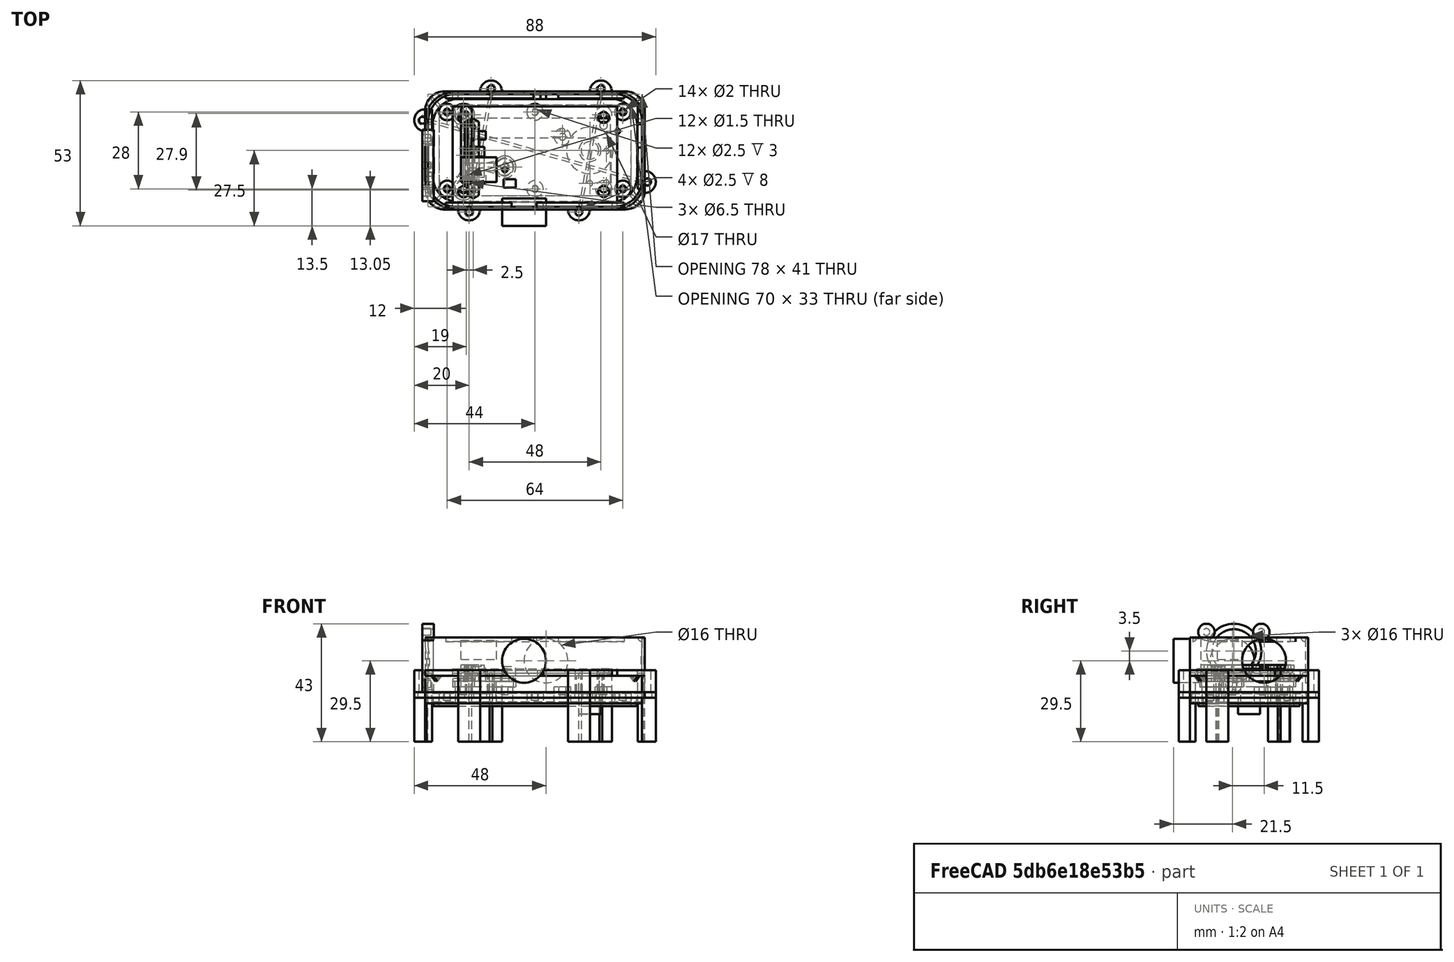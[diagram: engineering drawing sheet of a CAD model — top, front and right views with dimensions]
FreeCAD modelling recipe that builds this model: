
FCSTD DOCUMENT  (FreeCAD 0.18R4 (GitTag))
Label: control_sbox+deckel_166
License: All rights reserved
LicenseURL: http://en.wikipedia.org/wiki/All_rights_reserved
objects: Part::Cylinder×76, PartDesign::Body×49, Sketcher::SketchObject×48, PartDesign::Pad×48, App::DocumentObjectGroup×48, Part::Cut×36, Part::Box×27, App::Part×19, Mesh::Feature×13, Part::MultiFuse×6, PartDesign::Fillet×5
note: 343 computed .brp shape members not serialized (recipe doc carries the construction recipe); baked Part::Feature solids carry a one-line shape summary decoded from their .brp

FEATURE [Sketcher::SketchObject] Sketch001
  sketch-geometry (8):
    g0: LineSegment StartX=11 StartY=1.8e-15 StartZ=0 EndX=69 EndY=1.8e-15 EndZ=0
    g1: LineSegment StartX=80 StartY=11 StartZ=0 EndX=80 EndY=32 EndZ=0
    g2: LineSegment StartX=69 StartY=43 StartZ=0 EndX=11 EndY=43 EndZ=0
    g3: LineSegment StartX=0 StartY=32 StartZ=0 EndX=0 EndY=11 EndZ=0
    g4: ArcOfCircle CenterX=11 CenterY=32 CenterZ=0 NormalX=0 NormalY=0 NormalZ=1 AngleXU=0 Radius=11 StartAngle=1.5708 EndAngle=3.14159
    g5: ArcOfCircle CenterX=11 CenterY=11 CenterZ=0 NormalX=0 NormalY=0 NormalZ=1 AngleXU=0 Radius=11 StartAngle=3.14159 EndAngle=4.71239
    g6: ArcOfCircle CenterX=69 CenterY=32 CenterZ=0 NormalX=0 NormalY=0 NormalZ=1 AngleXU=0 Radius=11 StartAngle=1e-16 EndAngle=1.5708
    g7: ArcOfCircle CenterX=69 CenterY=11 CenterZ=0 NormalX=0 NormalY=0 NormalZ=1 AngleXU=0 Radius=11 StartAngle=4.71239 EndAngle=6.28319
  constraints (20):
    c: Horizontal(g0)
    c: Horizontal(g2)
    c: Vertical(g1)
    c: Vertical(g3)
    c: Tangent(g2,g4) = -1.5708
    c: Tangent(g3,g4) = -1.5708
    c: Tangent(g3,g5) = -1.5708
    c: Tangent(g0,g5) = -1.5708
    c: Radius(g4) = 11
    c: Radius(g5) = 11
    c: Tangent(g2,g6) = -1.5708
    c: Tangent(g1,g6) = -1.5708
    c: Tangent(g1,g7) = -1.5708
    c: Tangent(g0,g7) = -1.5708
    c: Radius(g7) = 11
    c: Radius(g6) = 11
    c: DistanceY(g0,g2) = 43
    c: DistanceX(g3,g1) = 80
    c: DistanceX(g3,g-1) = 0
    c: DistanceY(g-1,g0) = 0
FEATURE [PartDesign::Pad] Pad001
  Length = 1.5
  Length2 = 100
  Profile = -> Sketch001
  Type = 0
FEATURE [Part::Cylinder] Cylinder001  label="S01"
  Angle = 195
  AttacherType = Attacher::AttachEngine3D
  Height = 26
  Placement = pos=(2e-15,12.5,-14) rot=(0,0,1;1.309rad)
  Radius = 4
FEATURE [Part::Cylinder] Cylinder002  label="S10"
  Angle = 195
  AttacherType = Attacher::AttachEngine3D
  Height = 26
  Placement = pos=(40,5,-14) rot=(0,0,-1;1.8326rad)
  Radius = 4
FEATURE [Sketcher::SketchObject] Sketch028  label="Sketch029"
  MapMode = 5
  Support = -> [XY_Plane031]
  sketch-geometry (7):
    g0: LineSegment StartX=9.25 StartY=-0.000236886 StartZ=0 EndX=12 EndY=-0.000236886 EndZ=0
    g1: LineSegment StartX=12 StartY=-0.000236886 StartZ=0 EndX=12 EndY=5.0032 EndZ=0
    g2: LineSegment StartX=5 StartY=12.0032 StartZ=0 EndX=0.00298606 EndY=12.0032 EndZ=0
    g3: LineSegment StartX=0.00298606 StartY=12.0032 StartZ=0 EndX=0.00298606 EndY=9.25 EndZ=0
    g4: ArcOfCircle CenterX=0 CenterY=0 CenterZ=0 NormalX=0 NormalY=0 NormalZ=1 AngleXU=0 Radius=9.25 StartAngle=6.28316 EndAngle=7.85366
    g5: ArcOfCircle CenterX=5 CenterY=5.0032 CenterZ=0 NormalX=0 NormalY=0 NormalZ=1 AngleXU=0 Radius=7 StartAngle=0 EndAngle=1.5708
    g6: LineSegment [constr] StartX=0 StartY=0.00319501 StartZ=0 EndX=13.5092 EndY=13.5123 EndZ=0
  constraints (17):
    c: Coincident(g0,g1)
    c: Coincident(g2,g3)
    c: Horizontal(g0)
    c: Horizontal(g2)
    c: Vertical(g1)
    c: Vertical(g3)
    c: Coincident(g3,g4)
    c: Coincident(g0,g4)
    c: Tangent(g1,g5) = -1.5708
    c: Tangent(g2,g5) = -1.5708
    c: Radius(g5) = 7
    c: Coincident(g4,g-1)
    c: PointOnObject(g6,g-2)
    c: Angle(g-1,g6) = 0.785398
    c: PointOnObject(g5,g6)
    c: DistanceX(g4,g0) = 9.25
    c: DistanceX(g0,g0) = 2.75
FEATURE [PartDesign::Pad] Pad017
  Length = 2
  Length2 = 100
  Profile = -> Sketch028
  Type = 0
FEATURE [PartDesign::Body] Body031  label="SW"
  Group = -> [Sketch028,Pad017]
  Origin = -> Origin031
  Placement = pos=(12,12,10) rot=(0,0,1;3.14159rad)
  Tip = -> Pad017
FEATURE [Sketcher::SketchObject] Sketch027  label="Sketch028"
  MapMode = 5
  Support = -> [XY_Plane030]
  sketch-geometry (7):
    g0: LineSegment StartX=9.25 StartY=0 StartZ=0 EndX=12 EndY=0 EndZ=0
    g1: LineSegment StartX=12 StartY=0 StartZ=0 EndX=12 EndY=5 EndZ=0
    g2: LineSegment StartX=5 StartY=12 StartZ=0 EndX=3.20959e-05 EndY=12 EndZ=0
    g3: LineSegment StartX=3.20959e-05 StartY=12 StartZ=0 EndX=3.20959e-05 EndY=9.25 EndZ=0
    g4: ArcOfCircle CenterX=0 CenterY=0 CenterZ=0 NormalX=0 NormalY=0 NormalZ=1 AngleXU=0 Radius=9.25 StartAngle=0 EndAngle=1.57079
    g5: ArcOfCircle CenterX=5 CenterY=5 CenterZ=0 NormalX=0 NormalY=0 NormalZ=1 AngleXU=0 Radius=7 StartAngle=4.62e-14 EndAngle=1.5708
    g6: LineSegment [constr] StartX=0 StartY=0 StartZ=0 EndX=13.9782 EndY=13.9782 EndZ=0
  constraints (17):
    c: Coincident(g0,g1)
    c: Coincident(g2,g3)
    c: Horizontal(g0)
    c: Horizontal(g2)
    c: Vertical(g1)
    c: Vertical(g3)
    c: Coincident(g3,g4)
    c: Coincident(g0,g4)
    c: Tangent(g1,g5) = -1.5708
    c: Tangent(g2,g5) = -1.5708
    c: Coincident(g-1,g4)
    c: Coincident(g6,g4)
    c: Angle(g-1,g6) = 0.785398
    c: PointOnObject(g5,g6)
    c: DistanceX(g4,g0) = 9.25
    c: DistanceX(g0,g0) = 2.75
    c: Radius(g5) = 7
FEATURE [PartDesign::Pad] Pad016
  Length = 2
  Length2 = 100
  Profile = -> Sketch027
  Type = 0
FEATURE [PartDesign::Body] Body030  label="SO"
  Group = -> [Sketch027,Pad016]
  Origin = -> Origin030
  Placement = pos=(68,12,10) rot=(0,0,-1;1.5708rad)
  Tip = -> Pad016
FEATURE [Sketcher::SketchObject] Sketch026  label="Sketch027"
  MapMode = 5
  Support = -> [XY_Plane029]
  sketch-geometry (7):
    g0: LineSegment StartX=9.25 StartY=3.985e-13 StartZ=0 EndX=12 EndY=3.985e-13 EndZ=0
    g1: LineSegment StartX=12 StartY=3.985e-13 StartZ=0 EndX=12 EndY=5 EndZ=0
    g2: LineSegment StartX=5 StartY=12 StartZ=0 EndX=-3.3042e-05 EndY=12 EndZ=0
    g3: LineSegment StartX=-3.3042e-05 StartY=12 StartZ=0 EndX=-3.3042e-05 EndY=9.25 EndZ=0
    g4: ArcOfCircle CenterX=0 CenterY=0 CenterZ=0 NormalX=0 NormalY=0 NormalZ=1 AngleXU=0 Radius=9.25 StartAngle=4.31e-14 EndAngle=1.5708
    g5: ArcOfCircle CenterX=5 CenterY=5 CenterZ=0 NormalX=0 NormalY=0 NormalZ=1 AngleXU=0 Radius=7 StartAngle=0 EndAngle=1.5708
    g6: LineSegment [constr] StartX=0 StartY=0 StartZ=0 EndX=13.2062 EndY=13.2062 EndZ=0
  constraints (17):
    c: Coincident(g0,g1)
    c: Coincident(g2,g3)
    c: Horizontal(g0)
    c: Horizontal(g2)
    c: Vertical(g1)
    c: Vertical(g3)
    c: Coincident(g3,g4)
    c: Coincident(g0,g4)
    c: Tangent(g1,g5) = -1.5708
    c: Tangent(g2,g5) = -1.5708
    c: DistanceX(g0,g0) = 2.75
    c: Coincident(g4,g-1)
    c: DistanceX(g4,g0) = 9.25
    c: Coincident(g6,g4)
    c: Angle(g-1,g6) = 0.785398
    c: PointOnObject(g5,g6)
    c: Radius(g5) = 7
FEATURE [PartDesign::Pad] Pad015
  Length = 2
  Length2 = 100
  Profile = -> Sketch026
  Type = 0
FEATURE [PartDesign::Body] Body029  label="NW"
  Group = -> [Sketch026,Pad015]
  Origin = -> Origin029
  Placement = pos=(12,31,10) rot=(0,0,1;1.5708rad)
  Tip = -> Pad015
FEATURE [Sketcher::SketchObject] Sketch025  label="Sketch026"
  MapMode = 5
  Support = -> [XY_Plane028]
  sketch-geometry (7):
    g0: LineSegment StartX=9.25 StartY=-0.000167553 StartZ=0 EndX=12 EndY=-0.000167553 EndZ=0
    g1: LineSegment StartX=12 StartY=-0.000167553 StartZ=0 EndX=12 EndY=5 EndZ=0
    g2: LineSegment StartX=5 StartY=12 StartZ=0 EndX=0.00110554 EndY=12 EndZ=0
    g3: LineSegment StartX=0.00110554 StartY=12 StartZ=0 EndX=0.00110554 EndY=9.25 EndZ=0
    g4: ArcOfCircle CenterX=0 CenterY=0 CenterZ=0 NormalX=0 NormalY=0 NormalZ=1 AngleXU=0 Radius=9.25 StartAngle=6.28317 EndAngle=7.85386
    g5: ArcOfCircle CenterX=5 CenterY=5 CenterZ=0 NormalX=0 NormalY=0 NormalZ=1 AngleXU=0 Radius=7 StartAngle=0 EndAngle=1.5708
    g6: LineSegment [constr] StartX=0 StartY=0 StartZ=0 EndX=14.5776 EndY=14.5776 EndZ=0
  constraints (17):
    c: Coincident(g0,g1)
    c: Coincident(g2,g3)
    c: Horizontal(g0)
    c: Horizontal(g2)
    c: Vertical(g1)
    c: Vertical(g3)
    c: Coincident(g3,g4)
    c: Coincident(g0,g4)
    c: Tangent(g1,g5) = -1.5708
    c: Tangent(g2,g5) = -1.5708
    c: Radius(g5) = 7
    c: Coincident(g6,g4)
    c: Angle(g-1,g6) = 0.785398
    c: PointOnObject(g5,g6)
    c: Coincident(g-1,g4)
    c: DistanceX(g4,g0) = 9.25
    c: DistanceX(g0,g0) = 2.75
FEATURE [PartDesign::Pad] Pad014
  Length = 2
  Length2 = 100
  Profile = -> Sketch025
  Type = 0
FEATURE [PartDesign::Body] Body028  label="NO"
  Group = -> [Sketch025,Pad014]
  Origin = -> Origin028
  Placement = pos=(68,31,10) rot=(0,0,1;0rad)
  Tip = -> Pad014
FEATURE [Part::Box] Box006  label="N014"
  AttacherType = Attacher::AttachEngine3D
  Height = 2
  Length = 29
  Placement = pos=(42,0,10) rot=(0,0,1;0rad)
  Width = 2.75
FEATURE [Part::Box] Box004  label="W012"
  AttacherType = Attacher::AttachEngine3D
  Height = 2
  Length = 23
  Placement = pos=(2.75,-10,10) rot=(0,0,1;1.5708rad)
  Width = 2.75
FEATURE [Part::Box] Box007  label="O001"
  AttacherType = Attacher::AttachEngine3D
  Height = 2
  Length = 23
  Placement = pos=(40,5,10) rot=(0,0,1;1.5708rad)
  Width = 2.75
FEATURE [App::DocumentObjectGroup] Group005  label="Krümmung_F"
  Group = -> [Body028,Body029,Body030,Body031]
FEATURE [Part::Cylinder] Cylinder005  label="B_SO"
  Angle = 360
  AttacherType = Attacher::AttachEngine3D
  Height = 10
  Placement = pos=(41,5,4) rot=(0,0,1;0rad)
  Radius = 1.25
FEATURE [Part::Cylinder] Cylinder006  label="B_NW"
  Angle = 360
  AttacherType = Attacher::AttachEngine3D
  Height = 10
  Placement = pos=(-1,12.5,4) rot=(0,0,1;0rad)
  Radius = 1.25
FEATURE [Part::Cylinder] Cylinder007  label="B_NO"
  Angle = 360
  AttacherType = Attacher::AttachEngine3D
  Height = 10
  Placement = pos=(57,-1,4) rot=(0,0,1;0rad)
  Radius = 1.25
FEATURE [Part::Cylinder] Cylinder008  label="B_SW001"
  Angle = 360
  AttacherType = Attacher::AttachEngine3D
  Height = 5
  Placement = pos=(50,14,3) rot=(0,0,1;0rad)
  Radius = 1.25
FEATURE [Part::Cylinder] Cylinder009  label="001"
  Angle = 360
  AttacherType = Attacher::AttachEngine3D
  Height = 6
  Placement = pos=(10,14,0) rot=(0,0,1;0rad)
  Radius = 3
FEATURE [Part::Cylinder] Cylinder010  label="001001"
  Angle = 360
  AttacherType = Attacher::AttachEngine3D
  Height = 6
  Placement = pos=(30,14,0) rot=(0,0,1;0rad)
  Radius = 3
FEATURE [Part::MultiFuse] Fusion003
  Shapes = -> [Cylinder001,Box004]
FEATURE [Part::MultiFuse] Fusion004
  Shapes = -> [Cylinder002,Box007]
FEATURE [Sketcher::SketchObject] Sketch008
  MapMode = 5
  Support = -> [XY_Plane009]
  sketch-geometry (9):
    g0: LineSegment StartX=10 StartY=38.5 StartZ=0 EndX=70 EndY=38.5 EndZ=0
    g1: LineSegment StartX=70 StartY=38.5 StartZ=0 EndX=70 EndY=3.5 EndZ=0
    g2: LineSegment StartX=70 StartY=3.5 StartZ=0 EndX=10 EndY=3.5 EndZ=0
    g3: LineSegment StartX=10 StartY=3.5 StartZ=0 EndX=10 EndY=38.5 EndZ=0
    g4: Circle CenterX=14 CenterY=34.5 CenterZ=0 NormalX=0 NormalY=0 NormalZ=1 AngleXU=0 Radius=2
    g5: Circle CenterX=65 CenterY=34.5 CenterZ=0 NormalX=0 NormalY=0 NormalZ=1 AngleXU=0 Radius=2
    g6: Circle CenterX=65 CenterY=7.5 CenterZ=0 NormalX=0 NormalY=0 NormalZ=1 AngleXU=0 Radius=2
    g7: Circle CenterX=29 CenterY=15.5 CenterZ=0 NormalX=0 NormalY=0 NormalZ=1 AngleXU=0 Radius=1
    g8: Circle CenterX=13.99 CenterY=7.5 CenterZ=0 NormalX=0 NormalY=0 NormalZ=1 AngleXU=0 Radius=2
  constraints (27):
    c: Coincident(g0,g1)
    c: Coincident(g1,g2)
    c: Coincident(g2,g3)
    c: Coincident(g3,g0)
    c: Horizontal(g0)
    c: Horizontal(g2)
    c: Vertical(g1)
    c: Vertical(g3)
    c: DistanceY(g3,g3) = 35
    c: DistanceX(g0,g0) = 60
    c: Distance(g4,g3) = 4
    c: Distance(g-1,g2) = 3.5
    c: Distance(g-1,g3) = 10
    c: Diameter(g5) = 4
    c: Diameter(g4) = 4
    c: Diameter(g6) = 4
    c: Diameter(g7) = 2
    c: DistanceX(g4,g5) = 51
    c: DistanceX(g4,g6) = 51
    c: DistanceY(g-1,g7) = 15.5
    c: DistanceX(g4,g7) = 15
    c: Diameter(g8) = 4
    c: DistanceY(g8,g4) = 27
    c: DistanceY(g6,g5) = 27
    c: DistanceX(g8,g4) = 0.01
    c: DistanceY(g2,g8) = 4
    c: DistanceY(g2,g6) = 4
FEATURE [PartDesign::Pad] Pad005
  Length = 1.55
  Length2 = 100
  Profile = -> Sketch008
  Type = 0
FEATURE [PartDesign::Body] Body009  label="Platine"
  Group = -> [Sketch008,Pad005]
  Origin = -> Origin009
  Placement = pos=(0,-1,11) rot=(0,0,1;0rad)
  Tip = -> Pad005
FEATURE [Part::Box] Box028  label="USB Connector"
  AttacherType = Attacher::AttachEngine3D
  Height = 7
  Length = 13
  Placement = pos=(13,10,16) rot=(0,0,1;0rad)
  Width = 9
FEATURE [Part::Cylinder] Cylinder014  label="001001002"
  Angle = 360
  AttacherType = Attacher::AttachEngine3D
  Height = 6
  Placement = pos=(55,28,0) rot=(0,0,1;0rad)
  Radius = 3
FEATURE [Part::Cylinder] Cylinder017  label="B_SW006"
  Angle = 360
  AttacherType = Attacher::AttachEngine3D
  Height = 5
  Placement = pos=(10,14,3) rot=(0,0,1;0rad)
  Radius = 1.25
FEATURE [Part::Cylinder] Cylinder018  label="B_SW007"
  Angle = 360
  AttacherType = Attacher::AttachEngine3D
  Height = 5
  Placement = pos=(55,28,3) rot=(0,0,1;0rad)
  Radius = 1.25
FEATURE [Part::Cylinder] Cylinder019  label="001001003"
  Angle = 360
  AttacherType = Attacher::AttachEngine3D
  Height = 6
  Placement = pos=(50,14,0) rot=(0,0,1;0rad)
  Radius = 3
FEATURE [Part::Cylinder] Cylinder020  label="001001004"
  Angle = 360
  AttacherType = Attacher::AttachEngine3D
  Height = 6
  Placement = pos=(59,14,0) rot=(0,0,1;0rad)
  Radius = 3
FEATURE [Part::Cylinder] Cylinder021  label="B_SW008"
  Angle = 360
  AttacherType = Attacher::AttachEngine3D
  Height = 5
  Placement = pos=(59,14,3) rot=(0,0,1;0rad)
  Radius = 1.25
FEATURE [Part::Cylinder] Cylinder022  label="B_SW009"
  Angle = 360
  AttacherType = Attacher::AttachEngine3D
  Height = 5
  Placement = pos=(30,14,3) rot=(0,0,1;0rad)
  Radius = 1.25
FEATURE [Part::Cut] Cut  label="H_Cut"
  Base = -> Cylinder009
  Placement = pos=(19,1.5,0) rot=(0,0,1;0rad)
  Tool = -> Cylinder017
FEATURE [Part::Cut] Cut006  label="H_Cut006"
  Base = -> Cylinder010
  Placement = pos=(35,-6.5,0) rot=(0,0,1;0rad)
  Tool = -> Cylinder022
FEATURE [Part::Cut] Cut007  label="H_Cut007"
  Base = -> Cylinder014
  Placement = pos=(10,6.5,0) rot=(0,0,1;0rad)
  Tool = -> Cylinder018
FEATURE [Part::Cut] Cut008  label="H_Cut008"
  Base = -> Cylinder020
  Placement = pos=(-45,20.5,0) rot=(0,0,1;0rad)
  Tool = -> Cylinder021
FEATURE [Part::Cut] Cut009  label="H_Cut009"
  Base = -> Cylinder019
  Placement = pos=(-36,-6.5,0) rot=(0,0,1;0rad)
  Tool = -> Cylinder008
FEATURE [Part::Cylinder] Cylinder004  label="B_SW"
  Angle = 360
  AttacherType = Attacher::AttachEngine3D
  Height = 10
  Placement = pos=(10,-1,4) rot=(0,0,1;0rad)
  Radius = 1.25
FEATURE [Part::Box] Box005  label="S013"
  AttacherType = Attacher::AttachEngine3D
  Height = 2
  Length = 33
  Placement = pos=(4,0,10) rot=(0,0,1;0rad)
  Width = 2.75
FEATURE [Part::Cylinder] Cylinder  label="S00"
  Angle = 180
  AttacherType = Attacher::AttachEngine3D
  Height = 26
  Placement = pos=(10,0,-14) rot=(0,0,1;3.14159rad)
  Radius = 4
FEATURE [Part::Cut] Cut002  label="Cut002_O"
  Base = -> Fusion004
  Placement = pos=(40,5,0) rot=(0,0,1;0rad)
  Tool = -> Cylinder005
FEATURE [Part::Cut] Cut003  label="Cut003_W"
  Base = -> Fusion003
  Placement = pos=(0,20,0) rot=(0,0,1;0rad)
  Tool = -> Cylinder006
FEATURE [Part::Box] Box029  label="N015"
  AttacherType = Attacher::AttachEngine3D
  Height = 2
  Length = 28
  Placement = pos=(33,25.25,10) rot=(0,0,1;0rad)
  Width = 2.75
FEATURE [Part::Cylinder] Cylinder025  label="S014"
  Angle = 180
  AttacherType = Attacher::AttachEngine3D
  Height = 26
  Placement = pos=(11,28,-14) rot=(0,0,1;0rad)
  Radius = 4
FEATURE [Part::Cylinder] Cylinder026  label="B_NO001"
  Angle = 360
  AttacherType = Attacher::AttachEngine3D
  Height = 10
  Placement = pos=(55,29,4) rot=(0,0,1;0rad)
  Radius = 1.25
FEATURE [Part::Box] Box030  label="N016"
  AttacherType = Attacher::AttachEngine3D
  Height = 2
  Length = 34
  Placement = pos=(-3,25.25,10) rot=(0,0,1;0rad)
  Width = 2.75
FEATURE [Part::Cylinder] Cylinder027  label="S015"
  Angle = 180
  AttacherType = Attacher::AttachEngine3D
  Height = 26
  Placement = pos=(55,28,-14) rot=(0,0,1;0rad)
  Radius = 4
FEATURE [Part::Cylinder] Cylinder028  label="B_NO002"
  Angle = 360
  AttacherType = Attacher::AttachEngine3D
  Height = 10
  Placement = pos=(11,29,4) rot=(0,0,1;0rad)
  Radius = 1.25
FEATURE [Part::Cylinder] Cylinder029  label="S016"
  Angle = 180
  AttacherType = Attacher::AttachEngine3D
  Height = 26
  Placement = pos=(57,0,-14) rot=(0,0,1;3.14159rad)
  Radius = 4
FEATURE [Part::MultiFuse] Fusion
  Shapes = -> [Box029,Cylinder027]
FEATURE [Part::MultiFuse] Fusion005
  Shapes = -> [Cylinder025,Box030]
FEATURE [Part::Cut] Cut010  label="Cut010_NNO"
  Base = -> Fusion
  Placement = pos=(9,15,0) rot=(0,0,1;0rad)
  Tool = -> Cylinder026
FEATURE [Part::Cut] Cut011  label="Cut011_NNW"
  Base = -> Fusion005
  Placement = pos=(13,15,0) rot=(0,0,1;0rad)
  Tool = -> Cylinder028
FEATURE [Part::MultiFuse] Fusion008
  Shapes = -> [Box006,Cylinder029]
FEATURE [Part::Cut] Cut014  label="Cut014_SSO"
  Base = -> Fusion008
  Placement = pos=(-1,0,0) rot=(0,0,1;0rad)
  Tool = -> Cylinder007
FEATURE [Part::MultiFuse] Fusion009
  Shapes = -> [Cylinder,Box005]
FEATURE [Part::Cut] Cut015  label="Cut015_SSW"
  Base = -> Fusion009
  Placement = pos=(6,0,0) rot=(0,0,1;0rad)
  Tool = -> Cylinder004
FEATURE [Sketcher::SketchObject] Sketch034  label="Sketch035"
  MapMode = 5
  Support = -> [XY_Plane068]
  sketch-geometry (2):
    g0: Circle CenterX=0 CenterY=0 CenterZ=0 NormalX=0 NormalY=0 NormalZ=1 AngleXU=0 Radius=10
    g1: Circle CenterX=0 CenterY=0 CenterZ=0 NormalX=0 NormalY=0 NormalZ=1 AngleXU=0 Radius=8
  constraints (4):
    c: Coincident(g0,g-1)
    c: Radius(g0) = 10
    c: Coincident(g1,g0)
    c: Radius(g1) = 8
FEATURE [PartDesign::Pad] Pad021
  Length = 4
  Length2 = 100
  Profile = -> Sketch034
  Type = 0
FEATURE [PartDesign::Fillet] Fillet001
  Base = -> Pad021 [Edge5,Edge6]
  BaseFeature = -> Pad021
  Radius = 0.5
FEATURE [PartDesign::Body] Body037  label="Ring002"
  Group = -> [Sketch034,Pad021,Fillet001]
  Origin = -> Origin068
  Placement = pos=(-1,16,19) rot=(0,1,0;1.5708rad)
  Tip = -> Fillet001
FEATURE [App::DocumentObjectGroup] Gruppe033  label="Lock001"
FEATURE [App::DocumentObjectGroup] Gruppe034  label="Lock002"
FEATURE [App::DocumentObjectGroup] Gruppe032  label="Lock"
FEATURE [Part::Cylinder] Cylinder030  label="K0006"
  Angle = 360
  AttacherType = Attacher::AttachEngine3D
  Height = 4.1
  Placement = pos=(-1,6,26) rot=(0,1,0;1.5708rad)
  Radius = 3
FEATURE [Part::Cylinder] Cylinder031  label="K0007"
  Angle = 360
  AttacherType = Attacher::AttachEngine3D
  Height = 4.1
  Placement = pos=(-1,16,7) rot=(0,1,0;1.5708rad)
  Radius = 3
FEATURE [Part::Cylinder] Cylinder032  label="K0008"
  Angle = 360
  AttacherType = Attacher::AttachEngine3D
  Height = 4.1
  Placement = pos=(-1,26,26) rot=(0,1,0;1.5708rad)
  Radius = 3
FEATURE [Part::Box] Box025  label="std032"
  AttacherType = Attacher::AttachEngine3D
  Height = 1
  Length = 1
  Placement = pos=(3,16.5,4) rot=(0.57735,-0.57735,0.57735;2.0944rad)
  Width = 2
FEATURE [App::DocumentObjectGroup] Group014  label="DB_W_F"
  Group = -> [Body037,Gruppe032,Gruppe033,Box025,Gruppe034]
FEATURE [Part::Cylinder] Cylinder033  label="B_W"
  Angle = 360
  AttacherType = Attacher::AttachEngine3D
  Height = 10
  Placement = pos=(5,15.5,15.5) rot=(0,-1,0;1.5708rad)
  Radius = 8
FEATURE [Sketcher::SketchObject] Sketch
  MapMode = 5
  sketch-geometry (16):
    g0: LineSegment StartX=11 StartY=0 StartZ=0 EndX=69 EndY=0 EndZ=0
    g1: LineSegment StartX=80 StartY=11 StartZ=0 EndX=80 EndY=32 EndZ=0
    g2: LineSegment StartX=69 StartY=43 StartZ=0 EndX=11 EndY=43 EndZ=0
    g3: LineSegment StartX=0 StartY=32 StartZ=0 EndX=0 EndY=11 EndZ=0
    g4: LineSegment StartX=11 StartY=1 StartZ=0 EndX=69 EndY=1 EndZ=0
    g5: LineSegment StartX=79 StartY=11 StartZ=0 EndX=79 EndY=32 EndZ=0
    g6: LineSegment StartX=69 StartY=42 StartZ=0 EndX=11 EndY=42 EndZ=0
    g7: LineSegment StartX=1 StartY=32 StartZ=0 EndX=1 EndY=11 EndZ=0
    g8: ArcOfCircle CenterX=11 CenterY=32 CenterZ=0 NormalX=0 NormalY=0 NormalZ=1 AngleXU=0 Radius=10 StartAngle=1.5708 EndAngle=3.14159
    g9: ArcOfCircle CenterX=11 CenterY=11 CenterZ=0 NormalX=0 NormalY=0 NormalZ=1 AngleXU=0 Radius=10 StartAngle=3.14159 EndAngle=4.71239
    g10: ArcOfCircle CenterX=69 CenterY=11 CenterZ=0 NormalX=0 NormalY=0 NormalZ=1 AngleXU=0 Radius=10 StartAngle=4.71239 EndAngle=6.28319
    g11: ArcOfCircle CenterX=69 CenterY=32 CenterZ=0 NormalX=0 NormalY=0 NormalZ=1 AngleXU=0 Radius=10 StartAngle=0 EndAngle=1.5708
    g12: ArcOfCircle CenterX=69 CenterY=32 CenterZ=0 NormalX=0 NormalY=0 NormalZ=1 AngleXU=0 Radius=11 StartAngle=0 EndAngle=1.5708
    g13: ArcOfCircle CenterX=69 CenterY=11 CenterZ=0 NormalX=0 NormalY=0 NormalZ=1 AngleXU=0 Radius=11 StartAngle=4.71239 EndAngle=6.28319
    g14: ArcOfCircle CenterX=11 CenterY=32 CenterZ=0 NormalX=0 NormalY=0 NormalZ=1 AngleXU=0 Radius=11 StartAngle=1.5708 EndAngle=3.14159
    g15: ArcOfCircle CenterX=11 CenterY=11 CenterZ=0 NormalX=0 NormalY=0 NormalZ=1 AngleXU=0 Radius=11 StartAngle=3.14159 EndAngle=4.71239
  constraints (40):
    c: Horizontal(g0)
    c: Horizontal(g2)
    c: Vertical(g1)
    c: Vertical(g3)
    c: Horizontal(g4)
    c: Horizontal(g6)
    c: Vertical(g5)
    c: Vertical(g7)
    c: Tangent(g6,g8) = -1.5708
    c: Tangent(g7,g8) = -1.5708
    c: Tangent(g4,g9) = -1.5708
    c: Tangent(g7,g9) = -1.5708
    c: Tangent(g4,g10) = -1.5708
    c: Tangent(g5,g10) = -1.5708
    c: Tangent(g5,g11) = -1.5708
    c: Tangent(g6,g11) = -1.5708
    c: Tangent(g1,g12) = -1.5708
    c: Tangent(g2,g12) = -1.5708
    c: Tangent(g0,g13) = -1.5708
    c: Tangent(g1,g13) = -1.5708
    c: Tangent(g2,g14) = -1.5708
    c: Tangent(g3,g14) = -1.5708
    c: Tangent(g3,g15) = -1.5708
    c: Tangent(g0,g15) = -1.5708
    c: Radius(g8) = 10
    c: Radius(g9) = 10
    c: Radius(g14) = 11
    c: Radius(g11) = 10
    c: Radius(g10) = 10
    c: Radius(g12) = 11
    c: Radius(g13) = 11
    c: Radius(g15) = 11
    c: DistanceX(g3,g-1) = 0
    c: DistanceY(g0,g-1) = 0
    c: DistanceY(g0,g4) = 1
    c: DistanceX(g3,g7) = 1
    c: DistanceY(g0,g2) = 43
    c: DistanceY(g4,g6) = 41
    c: DistanceX(g7,g5) = 78
    c: DistanceX(g3,g1) = 80
FEATURE [PartDesign::Pad] Pad
  Length = 24
  Length2 = 100
  Profile = -> Sketch
  Type = 0
FEATURE [PartDesign::Body] Body  label="Rahmen_B"
  Origin = -> Origin002
  Placement = pos=(0,0,-13) rot=(0,0,1;0rad)
FEATURE [Part::Cylinder] Cylinder034  label="B_O"
  Angle = 360
  AttacherType = Attacher::AttachEngine3D
  Height = 10
  Placement = pos=(85,27,15.5) rot=(0,-1,0;1.5708rad)
  Radius = 8
FEATURE [Sketcher::SketchObject] Sketch036  label="Sketch037"
  MapMode = 5
  Support = -> [XY_Plane072]
  sketch-geometry (2):
    g0: Circle CenterX=0 CenterY=0 CenterZ=0 NormalX=0 NormalY=0 NormalZ=1 AngleXU=0 Radius=10
    g1: Circle CenterX=0 CenterY=0 CenterZ=0 NormalX=0 NormalY=0 NormalZ=1 AngleXU=0 Radius=8
  constraints (4):
    c: Coincident(g0,g-1)
    c: Radius(g0) = 10
    c: Coincident(g1,g0)
    c: Radius(g1) = 8
FEATURE [PartDesign::Pad] Pad023
  Length = 4
  Length2 = 100
  Profile = -> Sketch036
  Type = 0
FEATURE [PartDesign::Fillet] Fillet002
  Base = -> Pad023 [Edge5,Edge6]
  BaseFeature = -> Pad023
  Radius = 0.5
FEATURE [Part::Cylinder] Cylinder035  label="K0009"
  Angle = 360
  AttacherType = Attacher::AttachEngine3D
  Height = 4.1
  Placement = pos=(-1,6,26) rot=(0,1,0;1.5708rad)
  Radius = 3
FEATURE [Part::Cylinder] Cylinder036  label="K0010"
  Angle = 360
  AttacherType = Attacher::AttachEngine3D
  Height = 4.1
  Placement = pos=(-1,16,7) rot=(0,1,0;1.5708rad)
  Radius = 3
FEATURE [PartDesign::Body] Body039  label="Ring003"
  Group = -> [Sketch036,Pad023,Fillet002]
  Origin = -> Origin072
  Placement = pos=(-1,16,19) rot=(0,1,0;1.5708rad)
  Tip = -> Fillet002
FEATURE [Part::Cylinder] Cylinder037  label="K0011"
  Angle = 360
  AttacherType = Attacher::AttachEngine3D
  Height = 4.1
  Placement = pos=(-1,26,26) rot=(0,1,0;1.5708rad)
  Radius = 3
FEATURE [Part::Box] Box031  label="std033"
  AttacherType = Attacher::AttachEngine3D
  Height = 1
  Length = 1
  Placement = pos=(3,16.5,4) rot=(0.57735,-0.57735,0.57735;2.0944rad)
  Width = 2
FEATURE [App::DocumentObjectGroup] Gruppe058  label="Lock003"
FEATURE [App::DocumentObjectGroup] Gruppe059  label="Lock004"
FEATURE [App::DocumentObjectGroup] Gruppe060  label="Lock005"
FEATURE [App::DocumentObjectGroup] Group015  label="DB_E_F001"
  Group = -> [Body039,Gruppe060,Gruppe058,Box031,Gruppe059]
FEATURE [Sketcher::SketchObject] Sketch037  label="Sketch038"
  MapMode = 5
  Support = -> [XY_Plane075]
  sketch-geometry (2):
    g0: Circle CenterX=0 CenterY=0 CenterZ=0 NormalX=0 NormalY=0 NormalZ=1 AngleXU=0 Radius=10
    g1: Circle CenterX=0 CenterY=0 CenterZ=0 NormalX=0 NormalY=0 NormalZ=1 AngleXU=0 Radius=8
  constraints (4):
    c: Coincident(g0,g-1)
    c: Radius(g0) = 10
    c: Coincident(g1,g0)
    c: Radius(g1) = 8
FEATURE [PartDesign::Pad] Pad024
  Length = 4
  Length2 = 100
  Profile = -> Sketch037
  Type = 0
FEATURE [PartDesign::Fillet] Fillet003
  Base = -> Pad024 [Edge5,Edge6]
  BaseFeature = -> Pad024
  Radius = 0.5
FEATURE [Part::Cylinder] Cylinder038  label="K0012"
  Angle = 360
  AttacherType = Attacher::AttachEngine3D
  Height = 4.1
  Placement = pos=(-1,6,26) rot=(0,1,0;1.5708rad)
  Radius = 3
FEATURE [Part::Cylinder] Cylinder039  label="K0013"
  Angle = 360
  AttacherType = Attacher::AttachEngine3D
  Height = 4.1
  Placement = pos=(-1,16,7) rot=(0,1,0;1.5708rad)
  Radius = 3
FEATURE [PartDesign::Body] Body040  label="Ring004"
  Group = -> [Sketch037,Pad024,Fillet003]
  Origin = -> Origin075
  Placement = pos=(-1,16,19) rot=(0,1,0;1.5708rad)
  Tip = -> Fillet003
FEATURE [Part::Cylinder] Cylinder040  label="K0014"
  Angle = 360
  AttacherType = Attacher::AttachEngine3D
  Height = 4.1
  Placement = pos=(-1,26,26) rot=(0,1,0;1.5708rad)
  Radius = 3
FEATURE [Part::Box] Box032  label="std034"
  AttacherType = Attacher::AttachEngine3D
  Height = 1
  Length = 1
  Placement = pos=(3,16.5,4) rot=(0.57735,-0.57735,0.57735;2.0944rad)
  Width = 2
FEATURE [App::DocumentObjectGroup] Gruppe061  label="Lock006"
FEATURE [App::DocumentObjectGroup] Gruppe062  label="Lock007"
FEATURE [App::DocumentObjectGroup] Gruppe063  label="Lock008"
FEATURE [App::DocumentObjectGroup] Group016  label="DB_S_F002"
  Group = -> [Body040,Gruppe063,Gruppe061,Box032,Gruppe062]
FEATURE [Part::Cylinder] Cylinder041  label="B_S"
  Angle = 360
  AttacherType = Attacher::AttachEngine3D
  Height = 10
  Placement = pos=(36,4,15.5) rot=(0.57735,-0.57735,0.57735;2.0944rad)
  Radius = 8
FEATURE [Part::Cylinder] Cylinder042  label="B_N001"
  Angle = 360
  AttacherType = Attacher::AttachEngine3D
  Height = 10
  Placement = pos=(44,38,15.5) rot=(0.57735,0.57735,0.57735;4.18879rad)
  Radius = 8
FEATURE [Sketcher::SketchObject] Sketch038  label="Sketch039"
  MapMode = 5
  Support = -> [XY_Plane077]
  sketch-geometry (2):
    g0: Circle CenterX=0 CenterY=0 CenterZ=0 NormalX=0 NormalY=0 NormalZ=1 AngleXU=0 Radius=10
    g1: Circle CenterX=0 CenterY=0 CenterZ=0 NormalX=0 NormalY=0 NormalZ=1 AngleXU=0 Radius=8
  constraints (4):
    c: Coincident(g0,g-1)
    c: Radius(g0) = 10
    c: Coincident(g1,g0)
    c: Radius(g1) = 8
FEATURE [PartDesign::Pad] Pad025
  Length = 4
  Length2 = 100
  Profile = -> Sketch038
  Type = 0
FEATURE [PartDesign::Fillet] Fillet004
  Base = -> Pad025 [Edge5,Edge6]
  BaseFeature = -> Pad025
  Radius = 0.5
FEATURE [Part::Cylinder] Cylinder043  label="K0015"
  Angle = 360
  AttacherType = Attacher::AttachEngine3D
  Height = 4.1
  Placement = pos=(-1,6,26) rot=(0,1,0;1.5708rad)
  Radius = 3
FEATURE [Part::Cylinder] Cylinder044  label="K0016"
  Angle = 360
  AttacherType = Attacher::AttachEngine3D
  Height = 4.1
  Placement = pos=(-1,16,7) rot=(0,1,0;1.5708rad)
  Radius = 3
FEATURE [PartDesign::Body] Body041  label="Ring005"
  Group = -> [Sketch038,Pad025,Fillet004]
  Origin = -> Origin077
  Placement = pos=(-1,16,19) rot=(0,1,0;1.5708rad)
  Tip = -> Fillet004
FEATURE [Part::Cylinder] Cylinder045  label="K0017"
  Angle = 360
  AttacherType = Attacher::AttachEngine3D
  Height = 4.1
  Placement = pos=(-1,26,26) rot=(0,1,0;1.5708rad)
  Radius = 3
FEATURE [Part::Box] Box033  label="std035"
  AttacherType = Attacher::AttachEngine3D
  Height = 1
  Length = 1
  Placement = pos=(3,16.5,4) rot=(0.57735,-0.57735,0.57735;2.0944rad)
  Width = 2
FEATURE [App::DocumentObjectGroup] Gruppe064  label="Lock009"
FEATURE [App::DocumentObjectGroup] Gruppe065  label="Lock010"
FEATURE [App::DocumentObjectGroup] Gruppe066  label="Lock011"
FEATURE [App::DocumentObjectGroup] Group017  label="DB_W_F001"
  Group = -> [Body041,Gruppe066,Gruppe064,Box033,Gruppe065]
FEATURE [Part::Cylinder] Cylinder046  label="D015_SSO"
  Angle = 90
  AttacherType = Attacher::AttachEngine3D
  Height = 32
  Placement = pos=(72.5,1,24) rot=(0.57735,0.57735,-0.57735;4.18879rad)
  Radius = 1.5
FEATURE [Part::Cylinder] Cylinder047  label="D014_NNW"
  Angle = 90
  AttacherType = Attacher::AttachEngine3D
  Height = 32
  Placement = pos=(7.5,42,24) rot=(0.57735,-0.57735,0.57735;4.18879rad)
  Radius = 1.5
FEATURE [Part::Cylinder] Cylinder048  label="D013_WNW"
  Angle = 90
  AttacherType = Attacher::AttachEngine3D
  Height = 13
  Placement = pos=(1,23.5,24) rot=(-1,0,0;1.5708rad)
  Radius = 1.5
FEATURE [Part::Cylinder] Cylinder049  label="D013_WSW"
  Angle = 90
  AttacherType = Attacher::AttachEngine3D
  Height = 7
  Placement = pos=(1,6.5,24) rot=(-1,0,0;1.5708rad)
  Radius = 1.5
FEATURE [Part::Cylinder] Cylinder050  label="D015_SSW"
  Angle = 90
  AttacherType = Attacher::AttachEngine3D
  Height = 24
  Placement = pos=(31.5,1,24) rot=(0.57735,0.57735,-0.57735;4.18879rad)
  Radius = 1.5
FEATURE [Part::Cylinder] Cylinder051  label="D014_NNO"
  Angle = 90
  AttacherType = Attacher::AttachEngine3D
  Height = 24
  Placement = pos=(48.5,42,24) rot=(0.57735,-0.57735,0.57735;4.18879rad)
  Radius = 1.5
FEATURE [Part::Cylinder] Cylinder052  label="D012_OSO"
  Angle = 90
  AttacherType = Attacher::AttachEngine3D
  Height = 15
  Placement = pos=(79,22.5,24) rot=(0,0.707107,-0.707107;3.14159rad)
  Radius = 1.5
FEATURE [Part::Cylinder] Cylinder053  label="D012_ONO"
  Angle = 90
  AttacherType = Attacher::AttachEngine3D
  Height = 7
  Placement = pos=(79,38.5,24) rot=(0,0.707107,-0.707107;3.14159rad)
  Radius = 1.5
FEATURE [App::DocumentObjectGroup] Group018  label="Übergang_F"
  Group = -> [Cylinder046,Cylinder047,Cylinder048,Cylinder049,Cylinder050,Cylinder051,Cylinder052,Cylinder053]
FEATURE [App::Part] Part012  label="Übergang"
  Group = -> [Group018,Cylinder046,Cylinder047,Cylinder048,Cylinder049,Cylinder050,Cylinder051,Cylinder052,Cylinder053]
  Origin = -> Origin078
FEATURE [Part::Cylinder] Cylinder054  label="B_W001"
  Angle = 360
  AttacherType = Attacher::AttachEngine3D
  Height = 5
  Placement = pos=(2,16,7) rot=(0,-1,0;1.5708rad)
  Radius = 1.25
FEATURE [Part::Cylinder] Cylinder055  label="B_W002"
  Angle = 360
  AttacherType = Attacher::AttachEngine3D
  Height = 5
  Placement = pos=(2,6,26) rot=(0,-1,0;1.5708rad)
  Radius = 1.25
FEATURE [Part::Cylinder] Cylinder056  label="B_W003"
  Angle = 360
  AttacherType = Attacher::AttachEngine3D
  Height = 5
  Placement = pos=(2,26,26) rot=(0,-1,0;1.5708rad)
  Radius = 1.25
FEATURE [Part::Cut] Cut020
  Base = -> Cylinder030
  Tool = -> Cylinder055
FEATURE [Part::Cut] Cut021
  Base = -> Cylinder031
  Tool = -> Cylinder054
FEATURE [Part::Cut] Cut022
  Base = -> Cylinder032
  Tool = -> Cylinder056
FEATURE [App::DocumentObjectGroup] Group019  label="Bohrungen"
  Group = -> [Cut020,Cut021,Cut022]
FEATURE [App::Part] Part007  label="DB_W"
  Group = -> [Group014,Body037,Cylinder030,Gruppe032,Cylinder031,Gruppe033,Box025,Cylinder032,Gruppe034,Group019,Cylinder054,Cylinder055,Cylinder056,Cut020,Cut021,Cut022]
  Origin = -> Origin069
  Placement = pos=(0,-0.5,-17.5) rot=(0,0,1;0rad)
FEATURE [Part::Cylinder] Cylinder057  label="B_W004"
  Angle = 360
  AttacherType = Attacher::AttachEngine3D
  Height = 5
  Placement = pos=(2,26,26) rot=(0,-1,0;1.5708rad)
  Radius = 1.25
FEATURE [Part::Cylinder] Cylinder058  label="B_W005"
  Angle = 360
  AttacherType = Attacher::AttachEngine3D
  Height = 5
  Placement = pos=(2,16,7) rot=(0,-1,0;1.5708rad)
  Radius = 1.25
FEATURE [Part::Cylinder] Cylinder059  label="B_W006"
  Angle = 360
  AttacherType = Attacher::AttachEngine3D
  Height = 5
  Placement = pos=(2,6,26) rot=(0,-1,0;1.5708rad)
  Radius = 1.25
FEATURE [Part::Cylinder] Cylinder060  label="B_W007"
  Angle = 360
  AttacherType = Attacher::AttachEngine3D
  Height = 5
  Placement = pos=(2,16,7) rot=(0,-1,0;1.5708rad)
  Radius = 1.25
FEATURE [Part::Cylinder] Cylinder061  label="B_W008"
  Angle = 360
  AttacherType = Attacher::AttachEngine3D
  Height = 5
  Placement = pos=(2,26,26) rot=(0,-1,0;1.5708rad)
  Radius = 1.25
FEATURE [Part::Cylinder] Cylinder062  label="B_W009"
  Angle = 360
  AttacherType = Attacher::AttachEngine3D
  Height = 5
  Placement = pos=(2,6,26) rot=(0,-1,0;1.5708rad)
  Radius = 1.25
FEATURE [Part::Cylinder] Cylinder063  label="B_W010"
  Angle = 360
  AttacherType = Attacher::AttachEngine3D
  Height = 5
  Placement = pos=(5,6,26) rot=(0,-1,0;1.5708rad)
  Radius = 1.25
FEATURE [Part::Cylinder] Cylinder064  label="B_W011"
  Angle = 360
  AttacherType = Attacher::AttachEngine3D
  Height = 5
  Placement = pos=(5,26,26) rot=(0,-1,0;1.5708rad)
  Radius = 1.25
FEATURE [Part::Cylinder] Cylinder065  label="B_W012"
  Angle = 360
  AttacherType = Attacher::AttachEngine3D
  Height = 5
  Placement = pos=(5,16,7) rot=(0,-1,0;1.5708rad)
  Radius = 1.25
FEATURE [Part::Cut] Cut023
  Base = -> Cylinder038
  Tool = -> Cylinder062
FEATURE [Part::Cut] Cut024
  Base = -> Cylinder039
  Tool = -> Cylinder060
FEATURE [Part::Cut] Cut025
  Base = -> Cylinder040
  Tool = -> Cylinder061
FEATURE [App::DocumentObjectGroup] Group021  label="Bohrungen003"
  Group = -> [Cut023,Cut024,Cut025]
FEATURE [App::Part] Part010  label="DB_S"
  Group = -> [Body040,Gruppe061,Gruppe062,Gruppe063,Cylinder038,Cylinder039,Cylinder040,Box032,Group016,Group021,Cylinder060,Cylinder061,Cylinder062,Cut023,Cut024,Cut025]
  Origin = -> Origin074
  Placement = pos=(52,-4.9e-15,-17.5) rot=(0,0,1;1.5708rad)
FEATURE [Part::Cut] Cut026
  Base = -> Cylinder043
  Tool = -> Cylinder063
FEATURE [Part::Cut] Cut027
  Base = -> Cylinder044
  Tool = -> Cylinder065
FEATURE [Part::Cut] Cut028
  Base = -> Cylinder045
  Tool = -> Cylinder064
FEATURE [App::DocumentObjectGroup] Group022  label="Bohrungen004"
  Group = -> [Cut026,Cut027,Cut028]
FEATURE [App::Part] Part011  label="DB_N"
  Group = -> [Cylinder043,Cylinder044,Cylinder045,Box033,Body041,Gruppe065,Gruppe064,Gruppe066,Group017,Group022,Cylinder063,Cylinder064,Cylinder065,Cut026,Cut027,Cut028]
  Origin = -> Origin076
  Placement = pos=(60,41,-17.5) rot=(0,0,1;1.5708rad)
FEATURE [Part::Cut] Cut029
  Base = -> Cylinder035
  Tool = -> Cylinder059
FEATURE [Part::Cut] Cut030
  Base = -> Cylinder036
  Tool = -> Cylinder058
FEATURE [Part::Cut] Cut031
  Base = -> Cylinder037
  Tool = -> Cylinder057
FEATURE [App::DocumentObjectGroup] Group020  label="Bohrungen002"
  Group = -> [Cut029,Cut030,Cut031]
FEATURE [App::Part] Part009  label="DB_O"
  Group = -> [Group015,Body039,Cylinder035,Gruppe060,Cylinder036,Gruppe058,Box031,Cylinder037,Gruppe059,Group020,Cylinder057,Cylinder058,Cylinder059,Cut029,Cut030,Cut031]
  Origin = -> Origin073
  Placement = pos=(80,43,-17.5) rot=(0,0,1;3.14159rad)
FEATURE [App::DocumentObjectGroup] Group013  label="Durchbrüche"
  Group = -> [Part007,Part009,Part010,Part011]
FEATURE [Part::Box] Box015  label="std022"
  AttacherType = Attacher::AttachEngine3D
  Height = 3
  Length = 43
  Placement = pos=(17,0.5,0.5) rot=(0,0,1;1.39277rad)
  Width = 1
FEATURE [Part::Box] Box014  label="std021"
  AttacherType = Attacher::AttachEngine3D
  Height = 3
  Length = 82
  Placement = pos=(79.5,10.5,0.5) rot=(0,0,1;2.86409rad)
  Width = 1
FEATURE [Part::Box] Box012  label="std019"
  AttacherType = Attacher::AttachEngine3D
  Height = 3
  Length = 43
  Placement = pos=(57,0.5,0.5) rot=(0,0,1;1.39277rad)
  Width = 1
FEATURE [App::DocumentObjectGroup] Gruppe019  label="Rippen"
  Group = -> [Box012,Box014,Box015]
FEATURE [Part::Box] Box016  label="NNW"
  AttacherType = Attacher::AttachEngine3D
  Height = 2
  Length = 25
  Placement = pos=(24.5,43,-14) rot=(0.57735,-0.57735,0.57735;2.0944rad)
  Width = 1
FEATURE [Part::Box] Box034  label="NNE"
  AttacherType = Attacher::AttachEngine3D
  Height = 2
  Length = 25
  Placement = pos=(64.5,43,-14) rot=(0.57735,-0.57735,0.57735;2.0944rad)
  Width = 1
FEATURE [Part::Box] Box035  label="SSW"
  AttacherType = Attacher::AttachEngine3D
  Height = 2
  Length = 25
  Placement = pos=(17,2,-14) rot=(0.57735,-0.57735,0.57735;2.0944rad)
  Width = 1
FEATURE [Part::Box] Box036  label="SSE"
  AttacherType = Attacher::AttachEngine3D
  Height = 2
  Length = 25
  Placement = pos=(57,2,-14) rot=(0.57735,-0.57735,0.57735;2.0944rad)
  Width = 1
FEATURE [Part::Box] Box037  label="E"
  AttacherType = Attacher::AttachEngine3D
  Height = 2
  Length = 25
  Placement = pos=(77.5,10.5,-14) rot=(0.707107,0,0.707107;3.14159rad)
  Width = 1
FEATURE [Part::Box] Box038  label="W"
  AttacherType = Attacher::AttachEngine3D
  Height = 2
  Length = 25
  Placement = pos=(0.5,33,-14) rot=(0.707107,0,0.707107;3.14159rad)
  Width = 1
FEATURE [App::DocumentObjectGroup] Gruppe067  label="Rippen001"
  Group = -> [Box016,Box034,Box035,Box036,Box037,Box038]
FEATURE [App::DocumentObjectGroup] Group  label="Stützen"
  Group = -> [Cut002,Cut003,Cut010,Cut011,Cut014,Cut015,Gruppe067]
FEATURE [App::DocumentObjectGroup] Group023  label="Wände"
  Group = -> [Body]
FEATURE [Sketcher::SketchObject] Sketch039  label="Sketch040"
  MapMode = 5
  Placement = pos=(0,0,0) rot=(1,0,0;1.5708rad)
  Support = -> [XZ_Plane079]
  sketch-geometry (3):
    g0: LineSegment StartX=0 StartY=-2 StartZ=0 EndX=0 EndY=2 EndZ=0
    g1: LineSegment StartX=0 StartY=2 StartZ=0 EndX=2 EndY=-4e-16 EndZ=0
    g2: LineSegment StartX=2 StartY=-4e-16 StartZ=0 EndX=0 EndY=-2 EndZ=0
  constraints (6):
    c: Coincident(g0,g1)
    c: Coincident(g1,g2)
    c: Symmetric(g0,g0,g-1)
    c: Coincident(g2,g0)
    c: DistanceY(g0,g0) = 4
    c: PointOnObject(g0,g-2)
FEATURE [PartDesign::Pad] Pad026
  Length = 1
  Length2 = 100
  Placement = pos=(0,0,0) rot=(1,0,0;1.5708rad)
  Profile = -> Sketch039
  Type = 0
FEATURE [PartDesign::Body] Body042  label="K_rippe_NW"
  Group = -> [Sketch039,Pad026]
  Origin = -> Origin079
  Placement = pos=(4.1,39.41,10) rot=(0.357407,0.862856,-0.357407;1.71777rad)
  Tip = -> Pad026
FEATURE [Sketcher::SketchObject] Sketch040  label="Sketch041"
  MapMode = 5
  Placement = pos=(0,0,0) rot=(1,0,0;1.5708rad)
  Support = -> [XZ_Plane080]
  sketch-geometry (3):
    g0: LineSegment StartX=0 StartY=-2 StartZ=0 EndX=0 EndY=2 EndZ=0
    g1: LineSegment StartX=0 StartY=2 StartZ=0 EndX=2 EndY=0 EndZ=0
    g2: LineSegment StartX=2 StartY=0 StartZ=0 EndX=0 EndY=-2 EndZ=0
  constraints (7):
    c: Coincident(g0,g1)
    c: Coincident(g1,g2)
    c: Symmetric(g0,g0,g-1)
    c: DistanceY(g0,g0) = 4
    c: Coincident(g2,g0)
    c: DistanceX(g0,g1) = 2
    c: PointOnObject(g0,g-2)
FEATURE [PartDesign::Pad] Pad027
  Length = 1
  Length2 = 100
  Placement = pos=(0,0,0) rot=(1,0,0;1.5708rad)
  Profile = -> Sketch040
  Type = 0
FEATURE [PartDesign::Body] Body043  label="K_rippe_SW"
  Group = -> [Sketch040,Pad027]
  Origin = -> Origin080
  Placement = pos=(3.75,3.66,9.99999) rot=(-0.357406,0.862857,0.357407;1.71777rad)
  Tip = -> Pad027
FEATURE [Sketcher::SketchObject] Sketch041  label="Sketch042"
  MapMode = 5
  Placement = pos=(0,0,0) rot=(1,0,0;1.5708rad)
  Support = -> [XZ_Plane081]
  sketch-geometry (3):
    g0: LineSegment StartX=0 StartY=-2 StartZ=0 EndX=0 EndY=2 EndZ=0
    g1: LineSegment StartX=0 StartY=2 StartZ=0 EndX=2 EndY=0 EndZ=0
    g2: LineSegment StartX=2 StartY=0 StartZ=0 EndX=0 EndY=-2 EndZ=0
  constraints (7):
    c: Coincident(g0,g1)
    c: Coincident(g1,g2)
    c: DistanceX(g0,g1) = 2
    c: DistanceY(g0,g0) = 4
    c: Symmetric(g0,g0,g-1)
    c: PointOnObject(g0,g-2)
    c: Coincident(g2,g0)
FEATURE [PartDesign::Pad] Pad028
  Length = 1
  Length2 = 100
  Placement = pos=(0,0,0) rot=(1,0,0;1.5708rad)
  Profile = -> Sketch041
  Type = 0
FEATURE [PartDesign::Body] Body044  label="K_rippe_SE"
  Group = -> [Sketch041,Pad028]
  Origin = -> Origin081
  Placement = pos=(76.05,3.46,10) rot=(-0.678598,0.281085,0.678598;2.59356rad)
  Tip = -> Pad028
FEATURE [Sketcher::SketchObject] Sketch042  label="Sketch043"
  MapMode = 5
  Placement = pos=(0,0,0) rot=(1,0,0;1.5708rad)
  Support = -> [XZ_Plane082]
  sketch-geometry (3):
    g0: LineSegment StartX=0 StartY=-2 StartZ=0 EndX=0 EndY=2 EndZ=0
    g1: LineSegment StartX=0 StartY=2 StartZ=0 EndX=2 EndY=0 EndZ=0
    g2: LineSegment StartX=2 StartY=0 StartZ=0 EndX=0 EndY=-2 EndZ=0
  constraints (7):
    c: Coincident(g0,g1)
    c: Coincident(g1,g2)
    c: DistanceX(g0,g1) = 2
    c: DistanceY(g0,g0) = 4
    c: PointOnObject(g0,g-2)
    c: Symmetric(g0,g0,g-1)
    c: Coincident(g2,g0)
FEATURE [PartDesign::Pad] Pad029
  Length = 1
  Length2 = 100
  Placement = pos=(0,0,0) rot=(1,0,0;1.5708rad)
  Profile = -> Sketch042
  Type = 0
FEATURE [PartDesign::Body] Body045  label="K_rippe_NE"
  Group = -> [Sketch042,Pad029]
  Origin = -> Origin082
  Placement = pos=(76.5,38.61,9.99997) rot=(-0.678598,-0.281084,0.678599;3.68963rad)
  Tip = -> Pad029
FEATURE [App::DocumentObjectGroup] Group024  label="K_stützen"
  Group = -> [Body042,Body043,Body044,Body045]
FEATURE [App::Part] Part  label="Rahmen"
  Group = -> [Group,Box006,Box005,Cylinder,Box004,Cylinder001,Fusion003,Box007,Cylinder002,Fusion004,Cylinder005,Cut002,Cylinder006,Cut003,Cylinder004,Cylinder007,Body031,Body030,Body029,Body028,Group005,Box029,Cylinder025,Cylinder026,Box030,Cylinder027,Cylinder028,Cylinder029,Fusion,Fusion005,Cut010,Cut011,Fusion008,Cut014,Fusion009,Cut015,Group013,Part007,Part009,Part010,Part011,Gruppe067,Box016,Box034,+9 more]
  Origin = -> Origin
  Placement = pos=(0,0,14) rot=(0,0,1;0rad)
FEATURE [Part::Cut] Cut032
  Base = -> Pad
  Tool = -> Cylinder042
FEATURE [Part::Cut] Cut033
  Base = -> Cut032
  Tool = -> Cylinder034
FEATURE [Part::Cut] Cut034
  Base = -> Cut033
  Tool = -> Cylinder033
FEATURE [App::DocumentObjectGroup] Group009  label="Bohrungen001"
  Group = -> [Cylinder041,Cut034]
FEATURE [Part::Cut] Cut035  label="H_Cut035"
  Base = -> Cylinder009
  Placement = pos=(40,12.5,0) rot=(0,0,1;0rad)
  Tool = -> Cylinder017
FEATURE [App::DocumentObjectGroup] Group010  label="halterung"
  Group = -> [Cut,Cut006,Cut007,Cut008,Cut009,Cut035]
FEATURE [Sketcher::SketchObject] Sketch043  label="Sketch044"
  MapMode = 5
  Support = -> [XY_Plane084]
  sketch-geometry (23):
    g0: Circle CenterX=14 CenterY=34.5 CenterZ=0 NormalX=0 NormalY=0 NormalZ=1 AngleXU=0 Radius=3.25
    g1: Circle CenterX=14 CenterY=7.5 CenterZ=0 NormalX=0 NormalY=0 NormalZ=1 AngleXU=0 Radius=3.25
    g2: LineSegment [constr] StartX=14 StartY=48.9156 StartZ=0 EndX=14 EndY=-5.6741 EndZ=0
    g3: ArcOfCircle CenterX=14 CenterY=34.5 CenterZ=0 NormalX=0 NormalY=0 NormalZ=1 AngleXU=0 Radius=4 StartAngle=6e-16 EndAngle=3.64277
    g4: ArcOfCircle CenterX=14 CenterY=7.5 CenterZ=0 NormalX=0 NormalY=0 NormalZ=1 AngleXU=0 Radius=4 StartAngle=2.64041 EndAngle=6.28319
    g5: LineSegment [constr] StartX=-8.91239 StartY=15.5 StartZ=0 EndX=34.8006 EndY=15.5 EndZ=0
    g6: LineSegment StartX=18 StartY=17 StartZ=0 EndX=25.2919 EndY=17 EndZ=0
    g7: LineSegment StartX=25.2919 StartY=14 StartZ=0 EndX=18 EndY=14 EndZ=0
    g8: LineSegment [constr] StartX=18 StartY=14 StartZ=0 EndX=18 EndY=17 EndZ=0
    g9: LineSegment [constr] StartX=-0.860876 StartY=21 StartZ=0 EndX=35.3843 EndY=21 EndZ=0
    g10: LineSegment [constr] StartX=13 StartY=28 StartZ=0 EndX=18 EndY=28 EndZ=0
    g11: LineSegment [constr] StartX=18 StartY=28 StartZ=0 EndX=18 EndY=14 EndZ=0
    g12: LineSegment [constr] StartX=18 StartY=14 StartZ=0 EndX=13 EndY=14 EndZ=0
    g13: LineSegment [constr] StartX=13 StartY=14 StartZ=0 EndX=13 EndY=28 EndZ=0
    g14: LineSegment [constr] StartX=18 StartY=28 StartZ=0 EndX=18 EndY=17 EndZ=0
    g15: LineSegment StartX=13 StartY=28 StartZ=0 EndX=13 EndY=14 EndZ=0
    g16: LineSegment StartX=18 StartY=14 StartZ=0 EndX=18 EndY=7.5 EndZ=0
    g17: LineSegment StartX=13 StartY=14 StartZ=0 EndX=10.4919 EndY=9.42184 EndZ=0
    g18: LineSegment StartX=18 StartY=28 StartZ=0 EndX=18 EndY=34.5 EndZ=0
    g19: LineSegment StartX=13 StartY=28 StartZ=0 EndX=10.4919 EndY=32.5782 EndZ=0
    g20: LineSegment StartX=18 StartY=28 StartZ=0 EndX=18 EndY=17 EndZ=0
    g21: ArcOfCircle CenterX=29 CenterY=15.5 CenterZ=0 NormalX=0 NormalY=0 NormalZ=1 AngleXU=0 Radius=4 StartAngle=3.52599 EndAngle=9.04038
    g22: Circle CenterX=29 CenterY=15.5 CenterZ=0 NormalX=0 NormalY=0 NormalZ=1 AngleXU=0 Radius=3.25
  constraints (57):
    c: Radius(g0) = 3.25
    c: Radius(g1) = 3.25
    c: Coincident(g0,g3)
    c: Coincident(g1,g4)
    c: DistanceX(g-1,g2) = 14
    c: Horizontal(g5)
    c: DistanceY(g-1,g5) = 15.5
    c: Coincident(g7,g8)
    c: Coincident(g8,g6)
    c: Horizontal(g6)
    c: Horizontal(g7)
    c: Symmetric(g7,g6,g5)
    c: DistanceY(g7,g6) = 3
    c: Symmetric(g0,g1,g9)
    c: Coincident(g11,g12)
    c: Coincident(g12,g13)
    c: Coincident(g13,g10)
    c: Horizontal(g10)
    c: Vertical(g11)
    c: Vertical(g13)
    c: Coincident(g10,g11)
    c: Coincident(g11,g7)
    c: Radius(g4) = 4
    c: Symmetric(g12,g10,g9)
    c: DistanceX(g10,g10) = 5
    c: Vertical(g2)
    c: DistanceY(g-1,g1) = 7.5
    c: DistanceY(g1,g0) = 27
    c: PointOnObject(g1,g2)
    c: Coincident(g15,g10)
    c: Coincident(g15,g12)
    c: Coincident(g14,g6)
    c: Coincident(g14,g10)
    c: Coincident(g17,g15)
    c: Coincident(g16,g7)
    c: Coincident(g18,g10)
    c: Coincident(g19,g15)
    c: Coincident(g20,g6)
    c: Coincident(g20,g18)
    c: Radius(g3) = 4
    c: Coincident(g4,g17)
    c: Coincident(g16,g4)
    c: Coincident(g18,g3)
    c: Coincident(g19,g3)
    c: Tangent(g3,g18) = -1.5708
    c: Tangent(g3,g19) = 1.5708
    c: Tangent(g4,g16) = 1.5708
    c: Tangent(g4,g17) = -1.5708
    c: Horizontal(g12)
    c: DistanceX(g-1,g15) = 13
    c: PointOnObject(g21,g5)
    c: DistanceX(g2,g21) = 15
    c: Radius(g21) = 4
    c: Coincident(g6,g21)
    c: Coincident(g7,g21)
    c: Radius(g22) = 3.25
    c: Coincident(g22,g21)
FEATURE [PartDesign::Pad] Pad030
  Length = 2
  Length2 = 100
  Profile = -> Sketch043
  Type = 0
FEATURE [PartDesign::Body] Body046  label="Hüllen"
  Group = -> [Sketch043,Pad030]
  Origin = -> Origin084
  Placement = pos=(0,0,6) rot=(0,0,1;0rad)
  Tip = -> Pad030
FEATURE [App::Part] Part014  label="Platine-direct"
  Group = -> [Body009,Box028]
  Origin = -> Origin085
FEATURE [Sketcher::SketchObject] Sketch044  label="Sketch045"
  MapMode = 5
  Support = -> [XY_Plane087]
  sketch-geometry (10):
    g0: LineSegment StartX=0 StartY=0 StartZ=0 EndX=51.5 EndY=0 EndZ=0
    g1: LineSegment StartX=51.5 StartY=0 StartZ=0 EndX=51.5 EndY=21 EndZ=0
    g2: LineSegment StartX=51.5 StartY=21 StartZ=0 EndX=0 EndY=21 EndZ=0
    g3: LineSegment StartX=0 StartY=21 StartZ=0 EndX=0 EndY=0 EndZ=0
    g4: Circle CenterX=1.75 CenterY=16.25 CenterZ=0 NormalX=0 NormalY=0 NormalZ=1 AngleXU=0 Radius=1
    g5: Circle CenterX=1.75 CenterY=4.75 CenterZ=0 NormalX=0 NormalY=0 NormalZ=1 AngleXU=0 Radius=1
    g6: LineSegment [constr] StartX=-2.65934 StartY=10.5 StartZ=0 EndX=59.5243 EndY=10.5 EndZ=0
    g7: LineSegment [constr] StartX=25.75 StartY=27.6384 StartZ=0 EndX=25.75 EndY=-7.04752 EndZ=0
    g8: Circle CenterX=49.75 CenterY=16.25 CenterZ=0 NormalX=0 NormalY=0 NormalZ=1 AngleXU=0 Radius=1
    g9: Circle CenterX=49.75 CenterY=4.75 CenterZ=0 NormalX=0 NormalY=0 NormalZ=1 AngleXU=0 Radius=1
  constraints (22):
    c: Coincident(g0,g1)
    c: Coincident(g1,g2)
    c: Coincident(g2,g3)
    c: Coincident(g3,g0)
    c: Horizontal(g0)
    c: Horizontal(g2)
    c: Vertical(g1)
    c: Vertical(g3)
    c: DistanceY(g3,g3) = 21
    c: DistanceX(g0,g0) = 51.5
    c: Radius(g5) = 1
    c: Coincident(g0,g-1)
    c: Symmetric(g0,g2,g6)
    c: Symmetric(g5,g4,g6)
    c: DistanceY(g5,g4) = 11.5
    c: DistanceX(g0,g5) = 1.75
    c: Symmetric(g0,g0,g7)
    c: Symmetric(g8,g4,g7)
    c: Symmetric(g9,g5,g7)
    c: Equal(g5,g4)
    c: Equal(g4,g8)
    c: Equal(g8,g9)
FEATURE [PartDesign::Pad] Pad031
  Length = 1
  Length2 = 100
  Profile = -> Sketch044
  Type = 0
FEATURE [PartDesign::Body] Body047  label="plane"
  Group = -> [Sketch044,Pad031]
  Origin = -> Origin087
  Placement = pos=(16.25,5,10) rot=(0,0,1;0rad)
  Tip = -> Pad031
FEATURE [Part::Box] Box039  label="USB Connector001"
  AttacherType = Attacher::AttachEngine3D
  Height = 3
  Length = 6
  Placement = pos=(15.5,11.75,11) rot=(0,0,1;0rad)
  Width = 7.5
FEATURE [Sketcher::SketchObject] Sketch046  label="Sketch047"
  MapMode = 5
  Support = -> [XY_Plane091]
  sketch-geometry (31):
    g0: LineSegment [constr] StartX=-2.78551 StartY=16.5 StartZ=0 EndX=35.9831 EndY=16.5 EndZ=0
    g1: LineSegment [constr] StartX=18.5 StartY=38.2848 StartZ=0 EndX=18.5 EndY=1.20933 EndZ=0
    g2: Circle CenterX=18.5 CenterY=7.25 CenterZ=0 NormalX=0 NormalY=0 NormalZ=1 AngleXU=0 Radius=0.75
    g3: GeomPoint X=18.5 Y=7.25 Z=0
    g4: GeomPoint X=18.6 Y=22.25 Z=0
    g5: LineSegment [constr] StartX=15.9862 StartY=20.9487 StartZ=0 EndX=17 EndY=20.9487 EndZ=0
    g6: LineSegment [constr] StartX=12.0303 StartY=22.25 StartZ=0 EndX=19.3255 EndY=22.25 EndZ=0
    g7: LineSegment [constr] StartX=-4.22167 StartY=21 StartZ=0 EndX=42.5416 EndY=21 EndZ=0
    g8: Circle [constr] CenterX=14 CenterY=34.5 CenterZ=0 NormalX=0 NormalY=0 NormalZ=1 AngleXU=0 Radius=1.6
    g9: Circle [constr] CenterX=14 CenterY=7.5 CenterZ=0 NormalX=0 NormalY=0 NormalZ=1 AngleXU=0 Radius=1.6
    g10: LineSegment [constr] StartX=14 StartY=42.2647 StartZ=0 EndX=14 EndY=-1.81436 EndZ=0
    g11: LineSegment StartX=20.5 StartY=29.7859 StartZ=0 EndX=20.5 EndY=32.0953 EndZ=0
    g12: LineSegment StartX=20.5 StartY=32.0953 StartZ=0 EndX=18.5 EndY=33.25 EndZ=0
    g13: LineSegment StartX=18.5 StartY=33.25 StartZ=0 EndX=16.5 EndY=32.0953 EndZ=0
    g14: LineSegment StartX=16.5 StartY=32.0953 StartZ=0 EndX=16.5 EndY=29.7859 EndZ=0
    g15: LineSegment [constr] StartX=16.5 StartY=29.7859 StartZ=0 EndX=18.5 EndY=28.6312 EndZ=0
    g16: LineSegment [constr] StartX=18.5 StartY=28.6312 StartZ=0 EndX=20.5 EndY=29.7859 EndZ=0
    g17: Circle [constr] CenterX=18.5 CenterY=30.9406 CenterZ=0 NormalX=0 NormalY=0 NormalZ=1 AngleXU=0 Radius=2.3094
    g18: LineSegment StartX=20.5 StartY=5.4047 StartZ=0 EndX=20.5 EndY=7.7141 EndZ=0
    g19: LineSegment [constr] StartX=20.5 StartY=7.7141 StartZ=0 EndX=18.5 EndY=8.8688 EndZ=0
    g20: LineSegment [constr] StartX=18.5 StartY=8.8688 StartZ=0 EndX=16.5 EndY=7.7141 EndZ=0
    g21: LineSegment StartX=16.5 StartY=7.7141 StartZ=0 EndX=16.5 EndY=5.4047 EndZ=0
    g22: LineSegment StartX=16.5 StartY=5.4047 StartZ=0 EndX=18.5 EndY=4.25 EndZ=0
    g23: LineSegment StartX=18.5 StartY=4.25 StartZ=0 EndX=20.5 EndY=5.4047 EndZ=0
    g24: Circle [constr] CenterX=18.5 CenterY=6.5594 CenterZ=0 NormalX=0 NormalY=0 NormalZ=1 AngleXU=0 Radius=2.3094
    g25: LineSegment StartX=16.5 StartY=29.7859 StartZ=0 EndX=16.5 EndY=7.7141 EndZ=0
    g26: LineSegment StartX=20.5 StartY=29.7859 StartZ=0 EndX=20.5 EndY=7.7141 EndZ=0
    g27: Circle CenterX=18.5 CenterY=30.25 CenterZ=0 NormalX=0 NormalY=0 NormalZ=1 AngleXU=0 Radius=0.75
    g28: LineSegment [constr] StartX=6.75266 StartY=18.75 StartZ=0 EndX=35.0336 EndY=18.75 EndZ=0
    g29: Circle CenterX=18.5 CenterY=22.5 CenterZ=0 NormalX=0 NormalY=0 NormalZ=1 AngleXU=0 Radius=0.75
    g30: Circle CenterX=18.5 CenterY=11 CenterZ=0 NormalX=0 NormalY=0 NormalZ=1 AngleXU=0 Radius=0.75
  constraints (66):
    c: Vertical(g1)
    c: Horizontal(g0)
    c: DistanceX(g-1,g1) = 18.5
    c: Radius(g2) = 0.75
    c: PointOnObject(g2,g1)
    c: Coincident(g3,g2)
    c: Horizontal(g5)
    c: Horizontal(g6)
    c: Horizontal(g7)
    c: Radius(g9) = 1.6
    c: Radius(g8) = 1.6
    c: Vertical(g10)
    c: PointOnObject(g8,g10)
    c: DistanceX(g-1,g10) = 14
    c: DistanceY(g9,g8) = 27
    c: Symmetric(g9,g8,g7)
    c: DistanceY(g-1,g7) = 21
    c: DistanceY(g0,g7) = 4.5
    c: Coincident(g11,g12)
    c: Coincident(g12,g13)
    c: Coincident(g13,g14)
    c: Coincident(g14,g15)
    c: Coincident(g15,g16)
    c: Coincident(g16,g11)
    c: Equal(g11, g12-g16) x5
    c: PointOnObject(g11,g17)
    c: PointOnObject(g12,g17)
    c: PointOnObject(g13,g17)
    c: PointOnObject(g14,g17)
    c: PointOnObject(g15,g17)
    c: PointOnObject(g16,g17)
    c: Coincident(g18,g19)
    c: Coincident(g19,g20)
    c: Coincident(g20,g21)
    c: Coincident(g21,g22)
    c: Coincident(g22,g23)
    c: Coincident(g23,g18)
    c: Equal(g18, g19-g23) x5
    c: PointOnObject(g18,g24)
    c: PointOnObject(g19,g24)
    c: PointOnObject(g20,g24)
    c: PointOnObject(g21,g24)
    c: PointOnObject(g22,g24)
    c: PointOnObject(g23,g24)
    c: PointOnObject(g17,g1)
    c: PointOnObject(g15,g1)
    c: PointOnObject(g22,g1)
    c: Coincident(g26,g11)
    c: Coincident(g25,g14)
    c: Coincident(g26,g18)
    c: Coincident(g25,g20)
    c: DistanceX(g14,g11) = 4
    c: Vertical(g25)
    c: Radius(g27) = 0.75
    c: Vertical(g26)
    c: DistanceY(g22,g12) = 29
    c: Symmetric(g15,g19,g28)
    c: Symmetric(g2,g27,g28)
    c: DistanceY(g22,g2) = 3
    c: DistanceY(g-1,g28) = 18.75
    c: PointOnObject(g29,g1)
    c: PointOnObject(g30,g1)
    c: Radius(g29) = 0.75
    c: Radius(g30) = 0.75
    c: DistanceY(g30,g29) = 11.5
    c: DistanceY(g22,g30) = 6.75
FEATURE [PartDesign::Pad] Pad034
  Length = 6
  Length2 = 100
  Profile = -> Sketch046
  Type = 0
FEATURE [PartDesign::Body] Body050  label="Täger"
  Group = -> [Sketch046,Pad034]
  Origin = -> Origin091
  Placement = pos=(-1,-0.2,8) rot=(0,0,1;0rad)
  Tip = -> Pad034
FEATURE [Sketcher::SketchObject] Sketch048  label="Sketch049"
  MapMode = 5
  Support = -> [XY_Plane092]
  sketch-geometry (10):
    g0: LineSegment [constr] StartX=-6.93237 StartY=15.5 StartZ=0 EndX=36.7388 EndY=15.5 EndZ=0
    g1: LineSegment [constr] StartX=29 StartY=24.6884 StartZ=0 EndX=29 EndY=7.47839 EndZ=0
    g2: LineSegment StartX=14 StartY=17 StartZ=0 EndX=22 EndY=17 EndZ=0
    g3: LineSegment [constr] StartX=22 StartY=17 StartZ=0 EndX=22 EndY=14 EndZ=0
    g4: LineSegment StartX=22 StartY=14 StartZ=0 EndX=14 EndY=14 EndZ=0
    g5: LineSegment StartX=14 StartY=14 StartZ=0 EndX=14 EndY=17 EndZ=0
    g6: ArcOfCircle CenterX=29 CenterY=15.5 CenterZ=0 NormalX=0 NormalY=0 NormalZ=1 AngleXU=0 Radius=3 StartAngle=4.49107 EndAngle=8.0753
    g7: Circle CenterX=29 CenterY=15.5 CenterZ=0 NormalX=0 NormalY=0 NormalZ=1 AngleXU=0 Radius=1.6
    g8: LineSegment StartX=22 StartY=14 StartZ=0 EndX=28.3415 EndY=12.5732 EndZ=0
    g9: LineSegment StartX=22 StartY=17 StartZ=0 EndX=28.3415 EndY=18.4268 EndZ=0
  constraints (27):
    c: Horizontal(g0)
    c: DistanceY(g-1,g0) = 15.5
    c: Vertical(g1)
    c: DistanceX(g-1,g1) = 29
    c: Coincident(g2,g3)
    c: Coincident(g3,g4)
    c: Coincident(g4,g5)
    c: Coincident(g5,g2)
    c: Horizontal(g2)
    c: Horizontal(g4)
    c: Vertical(g3)
    c: Symmetric(g2,g4,g0)
    c: DistanceX(g-1,g4) = 14
    c: DistanceX(g4,g3) = 8
    c: PointOnObject(g6,g0)
    c: PointOnObject(g6,g1)
    c: Radius(g6) = 3
    c: Radius(g7) = 1.6
    c: PointOnObject(g7,g0)
    c: PointOnObject(g7,g1)
    c: Coincident(g9,g2)
    c: DistanceY(g5,g5) = 3
    c: Coincident(g8,g4)
    c: Coincident(g8,g6)
    c: Coincident(g9,g6)
    c: Tangent(g6,g9) = 1.5708
    c: Tangent(g6,g8) = -1.5708
FEATURE [PartDesign::Pad] Pad036
  Length = 2
  Length2 = 100
  Profile = -> Sketch048
  Type = 0
FEATURE [PartDesign::Body] Body051  label="Center_00"
  Group = -> [Sketch048,Pad036]
  Origin = -> Origin092
  Placement = pos=(0,0,8) rot=(0,0,1;0rad)
  Tip = -> Pad036
FEATURE [Sketcher::SketchObject] Sketch052  label="Sketch053"
  sketch-geometry (9):
    g0: Circle CenterX=60 CenterY=21.5 CenterZ=0 NormalX=0 NormalY=0 NormalZ=1 AngleXU=0 Radius=3.2
    g1: Circle CenterX=60 CenterY=21.5 CenterZ=0 NormalX=0 NormalY=0 NormalZ=1 AngleXU=0 Radius=4
    g2: LineSegment [constr] StartX=0 StartY=0 StartZ=0 EndX=80 EndY=0 EndZ=0
    g3: LineSegment [constr] StartX=80 StartY=0 StartZ=0 EndX=80 EndY=43 EndZ=0
    g4: LineSegment [constr] StartX=80 StartY=43 StartZ=0 EndX=0 EndY=43 EndZ=0
    g5: LineSegment [constr] StartX=0 StartY=43 StartZ=0 EndX=0 EndY=0 EndZ=0
    g6: LineSegment [constr] StartX=-5.90619 StartY=21.5 StartZ=0 EndX=88.4509 EndY=21.5 EndZ=0
    g7: LineSegment [constr] StartX=40 StartY=49.0379 StartZ=0 EndX=40 EndY=0 EndZ=0
    g8: LineSegment [constr] StartX=60 StartY=48.1934 StartZ=0 EndX=60 EndY=-6.88061 EndZ=0
  constraints (20):
    c: Radius(g0) = 3.2
    c: Radius(g1) = 4
    c: Coincident(g0,g1)
    c: Coincident(g2,g3)
    c: Coincident(g3,g4)
    c: Coincident(g4,g5)
    c: Coincident(g5,g2)
    c: Horizontal(g2)
    c: Horizontal(g4)
    c: Vertical(g3)
    c: Vertical(g5)
    c: Coincident(g2,g-1)
    c: DistanceY(g5,g5) = 43
    c: DistanceX(g2,g2) = 80
    c: Vertical(g8)
    c: Symmetric(g4,g-1,g6)
    c: Symmetric(g2,g-1,g7)
    c: Symmetric(g7,g2,g8)
    c: PointOnObject(g0,g6)
    c: PointOnObject(g0,g8)
FEATURE [Sketcher::SketchObject] Sketch053  label="Sketch054"
  MapMode = 5
  Support = -> [XY_Plane098]
  sketch-geometry (56):
    g0: ArcOfCircle CenterX=7 CenterY=36 CenterZ=0 NormalX=0 NormalY=0 NormalZ=1 AngleXU=0 Radius=7 StartAngle=1.5708 EndAngle=3.07011
    g1: ArcOfCircle CenterX=16 CenterY=0 CenterZ=0 NormalX=0 NormalY=0 NormalZ=1 AngleXU=0 Radius=4 StartAngle=3.14159 EndAngle=6.28319
    g2: ArcOfCircle CenterX=7 CenterY=7 CenterZ=0 NormalX=0 NormalY=0 NormalZ=1 AngleXU=0 Radius=7 StartAngle=3.14159 EndAngle=4.71239
    g3: Circle CenterX=24 CenterY=44 CenterZ=0 NormalX=0 NormalY=0 NormalZ=1 AngleXU=0 Radius=1.7
    g4: Circle CenterX=16 CenterY=-1 CenterZ=0 NormalX=0 NormalY=0 NormalZ=1 AngleXU=0 Radius=1.7
    g5: Circle CenterX=-1 CenterY=32.5 CenterZ=0 NormalX=0 NormalY=0 NormalZ=1 AngleXU=0 Radius=1.7
    g6: Circle CenterX=81.0827 CenterY=10 CenterZ=0 NormalX=0 NormalY=0 NormalZ=1 AngleXU=0 Radius=1.5
    g7: Circle CenterX=60 CenterY=21.5 CenterZ=0 NormalX=0 NormalY=0 NormalZ=1 AngleXU=0 Radius=8.5
    g8: LineSegment [constr] StartX=0 StartY=43 StartZ=0 EndX=80 EndY=43 EndZ=0
    g9: LineSegment [constr] StartX=80 StartY=43 StartZ=0 EndX=80 EndY=0 EndZ=0
    g10: LineSegment [constr] StartX=80 StartY=0 StartZ=0 EndX=0 EndY=0 EndZ=0
    g11: LineSegment [constr] StartX=0 StartY=0 StartZ=0 EndX=0 EndY=43 EndZ=0
    g12: LineSegment [constr] StartX=-5.43133 StartY=21.5 StartZ=0 EndX=84.9654 EndY=21.5 EndZ=0
    g13: LineSegment [constr] StartX=40 StartY=48.823 StartZ=0 EndX=40 EndY=0 EndZ=0
    g14: ArcOfCircle CenterX=73 CenterY=36 CenterZ=0 NormalX=0 NormalY=0 NormalZ=1 AngleXU=0 Radius=7 StartAngle=1e-16 EndAngle=1.5708
    g15: ArcOfCircle CenterX=73 CenterY=7 CenterZ=0 NormalX=0 NormalY=0 NormalZ=1 AngleXU=0 Radius=7 StartAngle=4.71239 EndAngle=6.13993
    g16: ArcOfCircle CenterX=56 CenterY=0 CenterZ=0 NormalX=0 NormalY=0 NormalZ=1 AngleXU=0 Radius=4 StartAngle=3.14159 EndAngle=6.28319
    g17: ArcOfCircle CenterX=64 CenterY=43 CenterZ=0 NormalX=0 NormalY=0 NormalZ=1 AngleXU=0 Radius=4 StartAngle=0 EndAngle=3.14159
    g18: ArcOfCircle CenterX=24 CenterY=43 CenterZ=0 NormalX=0 NormalY=0 NormalZ=1 AngleXU=0 Radius=4 StartAngle=0 EndAngle=3.14159
    g19: ArcOfCircle CenterX=0 CenterY=32.5 CenterZ=0 NormalX=0 NormalY=0 NormalZ=1 AngleXU=0 Radius=4 StartAngle=1.56633 EndAngle=4.71239
    g20: LineSegment [constr] StartX=-7.51757 StartY=32.5 StartZ=0 EndX=11.9155 EndY=32.5 EndZ=0
    g21: LineSegment [constr] StartX=69.2773 StartY=10 StartZ=0 EndX=87.091 EndY=10 EndZ=0
    g22: LineSegment [constr] StartX=24 StartY=49.4951 StartZ=0 EndX=24 EndY=34.8351 EndZ=0
    g23: LineSegment [constr] StartX=64 StartY=48.2166 StartZ=0 EndX=64 EndY=29.2949 EndZ=0
    g24: LineSegment [constr] StartX=56 StartY=6.19678 StartZ=0 EndX=56 EndY=-8.37805 EndZ=0
    g25: LineSegment [constr] StartX=16 StartY=3.46933 StartZ=0 EndX=16 EndY=-7.69619 EndZ=0
    g26: ArcOfCircle CenterX=80 CenterY=10 CenterZ=0 NormalX=0 NormalY=0 NormalZ=1 AngleXU=0 Radius=4 StartAngle=4.69446 EndAngle=7.85398
    g27: LineSegment [constr] StartX=-1 StartY=44 StartZ=0 EndX=81 EndY=44 EndZ=0
    g28: LineSegment [constr] StartX=81 StartY=44 StartZ=0 EndX=81 EndY=-1 EndZ=0
    g29: LineSegment [constr] StartX=81 StartY=-1 StartZ=0 EndX=-1 EndY=-1 EndZ=0
    g30: LineSegment [constr] StartX=-1 StartY=-1 StartZ=0 EndX=-1 EndY=44 EndZ=0
    g31: Circle CenterX=56 CenterY=-1 CenterZ=0 NormalX=0 NormalY=0 NormalZ=1 AngleXU=0 Radius=1.5
    g32: Circle CenterX=64 CenterY=44 CenterZ=0 NormalX=0 NormalY=0 NormalZ=1 AngleXU=0 Radius=1.7
    g33: LineSegment StartX=7 StartY=43 StartZ=0 EndX=20 EndY=43 EndZ=0
    g34: LineSegment StartX=28 StartY=43 StartZ=0 EndX=60 EndY=43 EndZ=0
    g35: LineSegment StartX=68 StartY=43 StartZ=0 EndX=73 EndY=43 EndZ=0
    g36: LineSegment StartX=80 StartY=36 StartZ=0 EndX=80 EndY=14 EndZ=0
    g37: LineSegment StartX=73 StartY=0 StartZ=0 EndX=60 EndY=0 EndZ=0
    g38: LineSegment StartX=52 StartY=0 StartZ=0 EndX=20 EndY=-1e-15 EndZ=0
    g39: LineSegment StartX=12 StartY=0 StartZ=0 EndX=7 EndY=0 EndZ=0
    g40: LineSegment StartX=0 StartY=7 StartZ=0 EndX=0 EndY=28.5 EndZ=0
    g41: LineSegment [constr] StartX=60 StartY=49.0378 StartZ=0 EndX=60 EndY=-12.7867 EndZ=0
    g42: Circle [constr] CenterX=60 CenterY=21.5 CenterZ=0 NormalX=0 NormalY=0 NormalZ=1 AngleXU=0 Radius=12
    g43: Circle CenterX=60 CenterY=9.5 CenterZ=0 NormalX=0 NormalY=0 NormalZ=1 AngleXU=0 Radius=1
    g44: Circle CenterX=50 CenterY=28.5 CenterZ=0 NormalX=0 NormalY=0 NormalZ=1 AngleXU=0 Radius=1
    g45: Circle CenterX=70 CenterY=28.5 CenterZ=0 NormalX=0 NormalY=0 NormalZ=1 AngleXU=0 Radius=1
    g46: Circle CenterX=40 CenterY=35.5 CenterZ=0 NormalX=0 NormalY=0 NormalZ=1 AngleXU=0 Radius=1
    g47: Circle CenterX=40 CenterY=7.5 CenterZ=0 NormalX=0 NormalY=0 NormalZ=1 AngleXU=0 Radius=1
    g48: Circle CenterX=8 CenterY=7.5 CenterZ=0 NormalX=0 NormalY=0 NormalZ=1 AngleXU=0 Radius=1
    g49: Circle CenterX=8 CenterY=35.5 CenterZ=0 NormalX=0 NormalY=0 NormalZ=1 AngleXU=0 Radius=1
    g50: Circle CenterX=72 CenterY=35.5 CenterZ=0 NormalX=0 NormalY=0 NormalZ=1 AngleXU=0 Radius=1
    g51: Circle CenterX=72 CenterY=7.5 CenterZ=0 NormalX=0 NormalY=0 NormalZ=1 AngleXU=0 Radius=1
    g52: LineSegment [constr] StartX=72 StartY=48.4781 StartZ=0 EndX=72 EndY=-5.31877 EndZ=0
    g53: LineSegment [constr] StartX=-7.84972 StartY=7.5 StartZ=0 EndX=93.6534 EndY=7.5 EndZ=0
    g54: LineSegment [constr] StartX=8 StartY=48.5649 StartZ=0 EndX=8 EndY=-4.49355 EndZ=0
    g55: LineSegment [constr] StartX=-9.04893 StartY=35.5 StartZ=0 EndX=87.8404 EndY=35.5 EndZ=0
  constraints (152):
    c: Radius(g0) = 7
    c: Radius(g1) = 4
    c: Radius(g3) = 1.7
    c: Radius(g4) = 1.7
    c: Radius(g5) = 1.7
    c: Radius(g6) = 1.5
    c: Radius(g7) = 8.5
    c: Coincident(g8,g9)
    c: Coincident(g9,g10)
    c: Coincident(g10,g11)
    c: Coincident(g11,g8)
    c: Horizontal(g8)
    c: Horizontal(g10)
    c: Vertical(g9)
    c: Vertical(g11)
    c: Coincident(g10,g-1)
    c: Symmetric(g-1,g8,g12)
    c: Symmetric(g2,g0,g12)
    c: Symmetric(g9,g-1,g13)
    c: Tangent(g2,g11) = 1.5708
    c: Tangent(g14,g9) = 1.5708
    c: PointOnObject(g1,g10)
    c: PointOnObject(g1,g10)
    c: Tangent(g0,g8) = 1.5708
    c: Tangent(g15,g10) = 1.5708
    c: Radius(g15) = 7
    c: Coincident(g19,g0)
    c: PointOnObject(g19,g11)
    c: Radius(g19) = 4
    c: Horizontal(g21)
    c: Horizontal(g20)
    c: Vertical(g23)
    c: Vertical(g22)
    c: Vertical(g25)
    c: Vertical(g24)
    c: DistanceX(g-1,g25) = 16
    c: DistanceX(g-1,g24) = 56
    c: DistanceX(g-1,g22) = 24
    c: DistanceX(g-1,g23) = 64
    c: DistanceY(g-1,g21) = 10
    c: DistanceY(g-1,g20) = 32.5
    c: PointOnObject(g5,g20)
    c: PointOnObject(g16,g24)
    c: PointOnObject(g16,g10)
    c: PointOnObject(g16,g10)
    c: Radius(g16) = 4
    c: PointOnObject(g18,g8)
    c: PointOnObject(g18,g8)
    c: PointOnObject(g18,g22)
    c: Radius(g18) = 4
    c: PointOnObject(g17,g8)
    c: PointOnObject(g17,g8)
    c: PointOnObject(g17,g23)
    c: Radius(g17) = 4
    c: Coincident(g26,g15)
    c: Tangent(g14,g8) = 1.5708
    c: Symmetric(g15,g14,g12)
    c: PointOnObject(g26,g9)
    c: PointOnObject(g26,g21)
    c: Radius(g26) = 4
    c: PointOnObject(g26,g9)
    c: PointOnObject(g19,g11)
    c: PointOnObject(g7,g12)
    c: PointOnObject(g6,g21)
    c: PointOnObject(g3,g22)
    c: Coincident(g27,g28)
    c: Coincident(g28,g29)
    c: Coincident(g29,g30)
    c: Coincident(g30,g27)
    c: Horizontal(g27)
    c: Horizontal(g29)
    c: Vertical(g28)
    c: Vertical(g30)
    c: DistanceY(g30,g30) = 45
    c: DistanceX(g29,g-1) = 1
    c: Tangent(g2,g10) = 1.5708
    c: DistanceY(g29,g-1) = 1
    c: PointOnObject(g4,g25)
    c: DistanceX(g29,g29) = 82
    c: PointOnObject(g3,g27)
    c: PointOnObject(g5,g30)
    c: PointOnObject(g4,g29)
    c: Radius(g32) = 1.7
    c: PointOnObject(g32,g23)
    c: PointOnObject(g32,g27)
    c: Radius(g31) = 1.5
    c: PointOnObject(g31,g24)
    c: PointOnObject(g31,g29)
    c: Coincident(g33,g0)
    c: Coincident(g33,g18)
    c: Coincident(g34,g18)
    c: Coincident(g34,g17)
    c: Coincident(g35,g17)
    c: Coincident(g35,g14)
    c: Coincident(g36,g14)
    c: Coincident(g36,g26)
    c: Coincident(g37,g15)
    c: Coincident(g37,g16)
    c: Coincident(g38,g16)
    c: Coincident(g38,g1)
    c: PointOnObject(g1,g25)
    c: Coincident(g39,g1)
    c: PointOnObject(g1,g38)
    c: PointOnObject(g16,g37)
    c: PointOnObject(g17,g8)
    c: PointOnObject(g18,g8)
    c: Coincident(g39,g2)
    c: Coincident(g40,g2)
    c: Coincident(g40,g19)
    c: PointOnObject(g19,g20)
    c: DistanceX(g-1,g13) = 40
    c: DistanceY(g-1,g12) = 21.5
    c: Vertical(g41)
    c: Symmetric(g13,g9,g41)
    c: PointOnObject(g7,g41)
    c: PointOnObject(g42,g12)
    c: PointOnObject(g42,g41)
    c: Radius(g42) = 12
    c: PointOnObject(g43,g41)
    c: PointOnObject(g43,g42)
    c: Radius(g43) = 1
    c: Radius(g44) = 1
    c: Radius(g45) = 1
    c: Symmetric(g44,g45,g41)
    c: DistanceX(g44,g7) = 10
    c: DistanceY(g7,g44) = 7
    c: Radius(g46) = 1
    c: PointOnObject(g46,g13)
    c: Radius(g47) = 1
    c: PointOnObject(g47,g13)
    c: Vertical(g52)
    c: DistanceX(g-1,g52) = 72
    c: Horizontal(g53)
    c: DistanceY(g53) = 7.5
    c: Vertical(g54)
    c: DistanceX(g-1,g54) = 8
    c: PointOnObject(g48,g53)
    c: PointOnObject(g48,g54)
    c: Radius(g49) = 1
    c: Radius(g48) = 1
    c: PointOnObject(g49,g54)
    c: Horizontal(g55)
    c: DistanceY(g-1,g55) = 35.5
    c: PointOnObject(g49,g55)
    c: Radius(g50) = 1
    c: PointOnObject(g50,g52)
    c: PointOnObject(g50,g55)
    c: Radius(g51) = 1
    c: PointOnObject(g51,g52)
    c: PointOnObject(g51,g53)
    c: PointOnObject(g47,g53)
    c: PointOnObject(g46,g55)
FEATURE [Sketcher::SketchObject] Sketch054  label="Sketch055"
  MapMode = 5
  Support = -> [XY_Plane099]
  sketch-geometry (18):
    g0: LineSegment StartX=12 StartY=3 StartZ=0 EndX=68 EndY=3 EndZ=0
    g1: LineSegment StartX=77 StartY=12 StartZ=0 EndX=77 EndY=31 EndZ=0
    g2: LineSegment StartX=68 StartY=40 StartZ=0 EndX=12 EndY=40 EndZ=0
    g3: LineSegment StartX=3 StartY=31 StartZ=0 EndX=3 EndY=12 EndZ=0
    g4: LineSegment StartX=12 StartY=5 StartZ=0 EndX=68 EndY=5 EndZ=0
    g5: LineSegment StartX=75 StartY=12 StartZ=0 EndX=75 EndY=31 EndZ=0
    g6: LineSegment StartX=68 StartY=38 StartZ=0 EndX=12 EndY=38 EndZ=0
    g7: LineSegment StartX=5 StartY=31 StartZ=0 EndX=5 EndY=12 EndZ=0
    g8: LineSegment [constr] StartX=-5.21574 StartY=21.5 StartZ=0 EndX=83.6914 EndY=21.5 EndZ=0
    g9: LineSegment [constr] StartX=40 StartY=48.2332 StartZ=0 EndX=40 EndY=-3.03633 EndZ=0
    g10: ArcOfCircle CenterX=12 CenterY=31 CenterZ=0 NormalX=0 NormalY=0 NormalZ=1 AngleXU=0 Radius=9 StartAngle=1.5708 EndAngle=3.14159
    g11: ArcOfCircle CenterX=68 CenterY=31 CenterZ=0 NormalX=0 NormalY=0 NormalZ=1 AngleXU=0 Radius=9 StartAngle=0 EndAngle=1.5708
    g12: ArcOfCircle CenterX=68 CenterY=12 CenterZ=0 NormalX=0 NormalY=0 NormalZ=1 AngleXU=0 Radius=9 StartAngle=4.71239 EndAngle=6.28319
    g13: ArcOfCircle CenterX=12 CenterY=12 CenterZ=0 NormalX=0 NormalY=0 NormalZ=1 AngleXU=0 Radius=9 StartAngle=3.14159 EndAngle=4.71239
    g14: ArcOfCircle CenterX=68 CenterY=31 CenterZ=0 NormalX=0 NormalY=0 NormalZ=1 AngleXU=0 Radius=7 StartAngle=0 EndAngle=1.5708
    g15: ArcOfCircle CenterX=68 CenterY=12 CenterZ=0 NormalX=0 NormalY=0 NormalZ=1 AngleXU=0 Radius=7 StartAngle=4.71239 EndAngle=6.28319
    g16: ArcOfCircle CenterX=12 CenterY=12 CenterZ=0 NormalX=0 NormalY=0 NormalZ=1 AngleXU=0 Radius=7 StartAngle=3.14159 EndAngle=4.71239
    g17: ArcOfCircle CenterX=12 CenterY=31 CenterZ=0 NormalX=0 NormalY=0 NormalZ=1 AngleXU=0 Radius=7 StartAngle=1.5708 EndAngle=3.14159
  constraints (38):
    c: Horizontal(g0)
    c: Horizontal(g2)
    c: Vertical(g1)
    c: Vertical(g3)
    c: Horizontal(g4)
    c: Vertical(g5)
    c: DistanceX(g-1,g9) = 40
    c: Vertical(g9)
    c: Tangent(g2,g10) = -1.5708
    c: Tangent(g3,g10) = -1.5708
    c: Tangent(g1,g11) = -1.5708
    c: Tangent(g2,g11) = -1.5708
    c: Tangent(g0,g12) = -1.5708
    c: Tangent(g1,g12) = -1.5708
    c: Tangent(g0,g13) = -1.5708
    c: Tangent(g3,g13) = -1.5708
    c: Symmetric(g1,g3,g9)
    c: Radius(g13) = 9
    c: Tangent(g5,g14) = -1.5708
    c: Tangent(g6,g14) = -1.5708
    c: Tangent(g4,g15) = -1.5708
    c: Tangent(g5,g15) = -1.5708
    c: Tangent(g4,g16) = -1.5708
    c: Tangent(g7,g16) = -1.5708
    c: Tangent(g6,g17) = -1.5708
    c: Tangent(g7,g17) = -1.5708
    c: Symmetric(g7,g5,g9)
    c: Vertical(g7)
    c: Radius(g15) = 7
    c: DistanceY(g-1,g8) = 21.5
    c: DistanceY(g-1,g0) = 3
    c: DistanceX(g-1,g3) = 3
    c: Symmetric(g14,g15,g8)
    c: Symmetric(g11,g12,g8)
    c: DistanceY(g0,g4) = 2
    c: Symmetric(g13,g10,g8)
    c: Symmetric(g17,g16,g8)
    c: DistanceX(g3,g7) = 2
FEATURE [PartDesign::Pad] Pad040
  Length = 3
  Length2 = 100
  Profile = -> Sketch054
  Type = 0
FEATURE [PartDesign::Body] Body056  label="dichtrahmen001"
  Group = -> [Sketch054,Pad040]
  Origin = -> Origin099
  Placement = pos=(0,0,-1) rot=(0,0,1;0rad)
  Tip = -> Pad040
FEATURE [PartDesign::Pad] Pad041
  Length = 6
  Length2 = 100
  Profile = -> Sketch052
  Type = 0
FEATURE [PartDesign::Body] Body055  label="anschluss001"
  Group = -> [Sketch052,Pad041]
  Origin = -> Origin100
  Placement = pos=(0,0,-4) rot=(0,0,1;0rad)
  Tip = -> Pad041
FEATURE [PartDesign::Pad] Pad042
  Length = 2
  Length2 = 100
  Profile = -> Sketch053
  Type = 0
FEATURE [PartDesign::Body] Body057  label="basis_ext001"
  Group = -> [Sketch053,Pad042]
  Origin = -> Origin097
  Placement = pos=(0,0,2) rot=(0,0,1;0rad)
  Tip = -> Pad042
FEATURE [App::DocumentObjectGroup] Gruppe069  label="Lock012"
FEATURE [App::DocumentObjectGroup] Gruppe070  label="Lock013"
FEATURE [Part::Cylinder] Cylinder070  label="K0018"
  Angle = 360
  AttacherType = Attacher::AttachEngine3D
  Height = 4.1
  Placement = pos=(-1,6,26) rot=(0,1,0;1.5708rad)
  Radius = 3
FEATURE [Part::Cylinder] Cylinder071  label="B_W013"
  Angle = 360
  AttacherType = Attacher::AttachEngine3D
  Height = 5
  Placement = pos=(2,6,26) rot=(0,-1,0;1.5708rad)
  Radius = 1.25
FEATURE [Part::Cylinder] Cylinder072  label="B_W014"
  Angle = 360
  AttacherType = Attacher::AttachEngine3D
  Height = 5
  Placement = pos=(2,26,26) rot=(0,-1,0;1.5708rad)
  Radius = 1.25
FEATURE [App::DocumentObjectGroup] Gruppe071  label="Lock014"
FEATURE [Sketcher::SketchObject] Sketch055  label="Sketch056"
  MapMode = 5
  Support = -> [XY_Plane102]
  sketch-geometry (2):
    g0: Circle CenterX=0 CenterY=0 CenterZ=0 NormalX=0 NormalY=0 NormalZ=1 AngleXU=0 Radius=10
    g1: Circle CenterX=0 CenterY=0 CenterZ=0 NormalX=0 NormalY=0 NormalZ=1 AngleXU=0 Radius=8
  constraints (4):
    c: Coincident(g0,g-1)
    c: Radius(g0) = 10
    c: Coincident(g1,g0)
    c: Radius(g1) = 8
FEATURE [Part::Cylinder] Cylinder073  label="B_W015"
  Angle = 360
  AttacherType = Attacher::AttachEngine3D
  Height = 5
  Placement = pos=(2,16,7) rot=(0,-1,0;1.5708rad)
  Radius = 1.25
FEATURE [Part::Cylinder] Cylinder075  label="K0020"
  Angle = 360
  AttacherType = Attacher::AttachEngine3D
  Height = 4.1
  Placement = pos=(-1,26,26) rot=(0,1,0;1.5708rad)
  Radius = 3
FEATURE [Part::Box] Box040  label="std036"
  AttacherType = Attacher::AttachEngine3D
  Height = 1
  Length = 1
  Placement = pos=(3,16.5,4) rot=(0.57735,-0.57735,0.57735;2.0944rad)
  Width = 2
FEATURE [Part::Cut] Cut038
  Base = -> Cylinder075
  Tool = -> Cylinder072
FEATURE [PartDesign::Pad] Pad043
  Length = 4
  Length2 = 100
  Profile = -> Sketch055
  Type = 0
FEATURE [PartDesign::Fillet] Fillet005
  Base = -> Pad043 [Edge5,Edge6]
  BaseFeature = -> Pad043
  Radius = 0.5
FEATURE [PartDesign::Body] Body058  label="Ring006"
  Group = -> [Sketch055,Pad043,Fillet005]
  Origin = -> Origin101
  Placement = pos=(-1,16,19) rot=(0,1,0;1.5708rad)
  Tip = -> Fillet005
FEATURE [App::DocumentObjectGroup] Group030  label="DB_W_F002"
  Group = -> [Body058,Gruppe071,Gruppe069,Box040,Gruppe070]
FEATURE [Part::Cylinder] Cylinder074  label="K0019"
  Angle = 360
  AttacherType = Attacher::AttachEngine3D
  Height = 4.1
  Placement = pos=(-1,16,7) rot=(0,1,0;1.5708rad)
  Radius = 3
FEATURE [Part::Cut] Cut037
  Base = -> Cylinder074
  Tool = -> Cylinder073
FEATURE [Part::Cut] Cut036
  Base = -> Cylinder070
  Tool = -> Cylinder071
FEATURE [App::DocumentObjectGroup] Group029  label="Bohrungen005"
  Group = -> [Cut036,Cut037,Cut038]
FEATURE [App::Part] Part018  label="DB_W001"
  Group = -> [Group030,Body058,Cylinder070,Gruppe071,Cylinder074,Gruppe069,Box040,Cylinder075,Gruppe070,Group029,Cylinder073,Cylinder071,Cylinder072,Cut036,Cut037,Cut038]
  Origin = -> Origin102
  Placement = pos=(76,2.5,3) rot=(-0.57735,0.57735,0.57735;2.0944rad)
FEATURE [Part::Cylinder] Cylinder076  label="B_W016"
  Angle = 360
  AttacherType = Attacher::AttachEngine3D
  Height = 5
  Placement = pos=(2,6,26) rot=(0,-1,0;1.5708rad)
  Radius = 1.25
FEATURE [Part::Cylinder] Cylinder077  label="K0021"
  Angle = 360
  AttacherType = Attacher::AttachEngine3D
  Height = 4.1
  Placement = pos=(-1,6,26) rot=(0,1,0;1.5708rad)
  Radius = 3
FEATURE [Part::Cut] Cut039  label="H_SW"
  Base = -> Cylinder077
  Placement = pos=(-18,1.5,3) rot=(0,1,0;1.5708rad)
  Tool = -> Cylinder076
FEATURE [Part::Cylinder] Cylinder078  label="K0022"
  Angle = 360
  AttacherType = Attacher::AttachEngine3D
  Height = 4.1
  Placement = pos=(-1,6,26) rot=(0,1,0;1.5708rad)
  Radius = 3
FEATURE [Part::Cylinder] Cylinder079  label="B_W017"
  Angle = 360
  AttacherType = Attacher::AttachEngine3D
  Height = 5
  Placement = pos=(2,6,26) rot=(0,-1,0;1.5708rad)
  Radius = 1.25
FEATURE [Part::Cut] Cut040  label="H_NW"
  Base = -> Cylinder078
  Placement = pos=(-18,29.5,3) rot=(0,1,0;1.5708rad)
  Tool = -> Cylinder079
FEATURE [Part::Cylinder] Cylinder080  label="K0023"
  Angle = 360
  AttacherType = Attacher::AttachEngine3D
  Height = 4.1
  Placement = pos=(-1,6,26) rot=(0,1,0;1.5708rad)
  Radius = 3
FEATURE [Part::Cylinder] Cylinder081  label="B_W018"
  Angle = 360
  AttacherType = Attacher::AttachEngine3D
  Height = 5
  Placement = pos=(2,6,26) rot=(0,-1,0;1.5708rad)
  Radius = 1.25
FEATURE [Part::Cut] Cut041  label="H_NO"
  Base = -> Cylinder080
  Placement = pos=(46,29.5,3) rot=(0,1,0;1.5708rad)
  Tool = -> Cylinder081
FEATURE [Part::Cylinder] Cylinder082  label="B_W019"
  Angle = 360
  AttacherType = Attacher::AttachEngine3D
  Height = 5
  Placement = pos=(2,6,26) rot=(0,-1,0;1.5708rad)
  Radius = 1.25
FEATURE [Part::Cylinder] Cylinder083  label="K0024"
  Angle = 360
  AttacherType = Attacher::AttachEngine3D
  Height = 4.1
  Placement = pos=(-1,6,26) rot=(0,1,0;1.5708rad)
  Radius = 3
FEATURE [Part::Cut] Cut042  label="H_SO"
  Base = -> Cylinder083
  Placement = pos=(46,1.5,3) rot=(0,1,0;1.5708rad)
  Tool = -> Cylinder082
FEATURE [Part::Cylinder] Cylinder084  label="B_W020"
  Angle = 360
  AttacherType = Attacher::AttachEngine3D
  Height = 5
  Placement = pos=(2,6,26) rot=(0,-1,0;1.5708rad)
  Radius = 1.25
FEATURE [Part::Cylinder] Cylinder085  label="K0025"
  Angle = 360
  AttacherType = Attacher::AttachEngine3D
  Height = 4.1
  Placement = pos=(-1,6,26) rot=(0,1,0;1.5708rad)
  Radius = 3
FEATURE [Part::Cut] Cut043  label="H_S"
  Base = -> Cylinder085
  Placement = pos=(14,1.5,3) rot=(0,1,0;1.5708rad)
  Tool = -> Cylinder084
FEATURE [Part::Cylinder] Cylinder086  label="B_W021"
  Angle = 360
  AttacherType = Attacher::AttachEngine3D
  Height = 5
  Placement = pos=(2,6,26) rot=(0,-1,0;1.5708rad)
  Radius = 1.25
FEATURE [Part::Cylinder] Cylinder087  label="K0026"
  Angle = 360
  AttacherType = Attacher::AttachEngine3D
  Height = 4.1
  Placement = pos=(-1,6,26) rot=(0,1,0;1.5708rad)
  Radius = 3
FEATURE [Part::Cut] Cut044  label="H_N"
  Base = -> Cylinder087
  Placement = pos=(14,29.5,3) rot=(0,1,0;1.5708rad)
  Tool = -> Cylinder086
FEATURE [App::DocumentObjectGroup] Group031  label="Halterung"
  Group = -> [Cut039,Cut040,Cut041,Cut042,Cut043,Cut044]
FEATURE [App::Part] Part017  label="Deckel002"
  Group = -> [Body056,Body055,Body057,Part018,Group031,Cylinder077,Cylinder076,Cut039,Cylinder078,Cylinder079,Cut040,Cylinder081,Cylinder080,Cut041,Cylinder082,Cylinder083,Cut042,Cylinder084,Cylinder085,Cut043,Cylinder086,Cylinder087,Cut044]
  Origin = -> Origin098
  Placement = pos=(0,0,24) rot=(0,0,1;0rad)
FEATURE [PartDesign::Body] Body001
  Origin = -> Origin003
FEATURE [PartDesign::Body] Body059
  Origin = -> Origin103
FEATURE [App::Part] Part001  label="Boden"
  Group = -> [Body001,Group010,Pad001,Sketch001,Cylinder009,Cylinder017,Cut,Cylinder010,Cylinder022,Cut006,Cylinder014,Cylinder018,Cut007,Cylinder020,Cylinder021,Cut008,Cylinder008,Cylinder019,Cut009,Box014,Box015,Box012,Gruppe019,Cut035,Body059]
  Origin = -> Origin001
FEATURE [App::Part] Part004  label="BOX"
  Group = -> [Part,Part001,Group009,Part012,Cylinder033,Cylinder034,Cylinder041,Cylinder042,Pad,Sketch,Group023,Body,Cut032,Cut033,Cut034]
  Origin = -> Origin034
FEATURE [Sketcher::SketchObject] Sketch058  label="Sketch059"
  MapMode = 5
  Support = -> [XY_Plane106]
  sketch-geometry (2):
    g0: Circle CenterX=14 CenterY=7.5 CenterZ=0 NormalX=0 NormalY=0 NormalZ=1 AngleXU=0 Radius=4
    g1: Circle CenterX=14 CenterY=7.5 CenterZ=0 NormalX=0 NormalY=0 NormalZ=1 AngleXU=0 Radius=1.6
  constraints (5):
    c: DistanceY(g-1,g0) = 7.5
    c: DistanceX(g-1,g0) = 14
    c: Coincident(g1,g0)
    c: Radius(g0) = 4
    c: Radius(g1) = 1.6
FEATURE [PartDesign::Pad] Pad046
  Length = 1
  Length2 = 100
  Profile = -> Sketch058
  Type = 0
FEATURE [PartDesign::Body] Body062  label="ab_S004"
  Group = -> [Sketch058,Pad046]
  Origin = -> Origin106
  Placement = pos=(0,0,8) rot=(0,0,1;0rad)
  Tip = -> Pad046
FEATURE [Sketcher::SketchObject] Sketch059  label="Sketch060"
  MapMode = 5
  Support = -> [XY_Plane107]
  sketch-geometry (2):
    g0: Circle CenterX=14 CenterY=7.5 CenterZ=0 NormalX=0 NormalY=0 NormalZ=1 AngleXU=0 Radius=4
    g1: Circle CenterX=14 CenterY=7.5 CenterZ=0 NormalX=0 NormalY=0 NormalZ=1 AngleXU=0 Radius=1.6
  constraints (5):
    c: DistanceY(g-1,g0) = 7.5
    c: DistanceX(g-1,g0) = 14
    c: Coincident(g1,g0)
    c: Radius(g0) = 4
    c: Radius(g1) = 1.6
FEATURE [PartDesign::Pad] Pad047
  Length = 1
  Length2 = 100
  Profile = -> Sketch059
  Type = 0
FEATURE [PartDesign::Body] Body063  label="ab_N003"
  Group = -> [Sketch059,Pad047]
  Origin = -> Origin107
  Placement = pos=(0,27,8) rot=(0,0,1;0rad)
  Tip = -> Pad047
FEATURE [Sketcher::SketchObject] Sketch060  label="Sketch061"
  MapMode = 5
  Support = -> [XY_Plane108]
  sketch-geometry (2):
    g0: Circle CenterX=14 CenterY=7.5 CenterZ=0 NormalX=0 NormalY=0 NormalZ=1 AngleXU=0 Radius=4
    g1: Circle CenterX=14 CenterY=7.5 CenterZ=0 NormalX=0 NormalY=0 NormalZ=1 AngleXU=0 Radius=1.6
  constraints (5):
    c: DistanceY(g-1,g0) = 7.5
    c: DistanceX(g-1,g0) = 14
    c: Coincident(g1,g0)
    c: Radius(g0) = 4
    c: Radius(g1) = 1.6
FEATURE [PartDesign::Pad] Pad048
  Length = 1
  Length2 = 100
  Profile = -> Sketch060
  Type = 0
FEATURE [PartDesign::Body] Body064  label="ab_C004"
  Group = -> [Sketch060,Pad048]
  Origin = -> Origin108
  Placement = pos=(15,8,8) rot=(0,0,1;0rad)
  Tip = -> Pad048
FEATURE [App::DocumentObjectGroup] Group026  label="abdeckung"
  Group = -> [Body062,Body063,Body064]
FEATURE [Part::Box] Box  label="versteifung"
  AttacherType = Attacher::AttachEngine3D
  Height = 2
  Length = 1.6
  Placement = pos=(14,11,8) rot=(0,0,1;0rad)
  Width = 20
FEATURE [App::Part] Part013  label="Träger_W"
  Group = -> [Body046,Body050,Body051,Group026,Body062,Body063,Body064,Box]
  Origin = -> Origin083
  Placement = pos=(0,0,-2) rot=(0,0,1;0rad)
FEATURE [Sketcher::SketchObject] Sketch061  label="Sketch062"
  MapMode = 5
  Support = -> [XY_Plane110]
  sketch-geometry (23):
    g0: Circle CenterX=14 CenterY=34.5 CenterZ=0 NormalX=0 NormalY=0 NormalZ=1 AngleXU=0 Radius=3.25
    g1: Circle CenterX=14 CenterY=7.5 CenterZ=0 NormalX=0 NormalY=0 NormalZ=1 AngleXU=0 Radius=3.25
    g2: LineSegment [constr] StartX=14 StartY=48.9156 StartZ=0 EndX=14 EndY=-5.6741 EndZ=0
    g3: ArcOfCircle CenterX=14 CenterY=34.5 CenterZ=0 NormalX=0 NormalY=0 NormalZ=1 AngleXU=0 Radius=4 StartAngle=6e-16 EndAngle=3.64277
    g4: ArcOfCircle CenterX=14 CenterY=7.5 CenterZ=0 NormalX=0 NormalY=0 NormalZ=1 AngleXU=0 Radius=4 StartAngle=2.64041 EndAngle=6.28319
    g5: LineSegment [constr] StartX=-8.91239 StartY=15.5 StartZ=0 EndX=34.8006 EndY=15.5 EndZ=0
    g6: LineSegment StartX=18 StartY=17 StartZ=0 EndX=25.2919 EndY=17 EndZ=0
    g7: LineSegment StartX=25.2919 StartY=14 StartZ=0 EndX=18 EndY=14 EndZ=0
    g8: LineSegment [constr] StartX=18 StartY=14 StartZ=0 EndX=18 EndY=17 EndZ=0
    g9: LineSegment [constr] StartX=-0.860876 StartY=21 StartZ=0 EndX=35.3843 EndY=21 EndZ=0
    g10: LineSegment [constr] StartX=13 StartY=28 StartZ=0 EndX=18 EndY=28 EndZ=0
    g11: LineSegment [constr] StartX=18 StartY=28 StartZ=0 EndX=18 EndY=14 EndZ=0
    g12: LineSegment [constr] StartX=18 StartY=14 StartZ=0 EndX=13 EndY=14 EndZ=0
    g13: LineSegment [constr] StartX=13 StartY=14 StartZ=0 EndX=13 EndY=28 EndZ=0
    g14: LineSegment [constr] StartX=18 StartY=28 StartZ=0 EndX=18 EndY=17 EndZ=0
    g15: LineSegment StartX=13 StartY=28 StartZ=0 EndX=13 EndY=14 EndZ=0
    g16: LineSegment StartX=18 StartY=14 StartZ=0 EndX=18 EndY=7.5 EndZ=0
    g17: LineSegment StartX=13 StartY=14 StartZ=0 EndX=10.4919 EndY=9.42184 EndZ=0
    g18: LineSegment StartX=18 StartY=28 StartZ=0 EndX=18 EndY=34.5 EndZ=0
    g19: LineSegment StartX=13 StartY=28 StartZ=0 EndX=10.4919 EndY=32.5782 EndZ=0
    g20: LineSegment StartX=18 StartY=28 StartZ=0 EndX=18 EndY=17 EndZ=0
    g21: ArcOfCircle CenterX=29 CenterY=15.5 CenterZ=0 NormalX=0 NormalY=0 NormalZ=1 AngleXU=0 Radius=4 StartAngle=3.52599 EndAngle=9.04038
    g22: Circle CenterX=29 CenterY=15.5 CenterZ=0 NormalX=0 NormalY=0 NormalZ=1 AngleXU=0 Radius=3.25
  constraints (57):
    c: Radius(g0) = 3.25
    c: Radius(g1) = 3.25
    c: Coincident(g0,g3)
    c: Coincident(g1,g4)
    c: DistanceX(g-1,g2) = 14
    c: Horizontal(g5)
    c: DistanceY(g-1,g5) = 15.5
    c: Coincident(g7,g8)
    c: Coincident(g8,g6)
    c: Horizontal(g6)
    c: Horizontal(g7)
    c: Symmetric(g7,g6,g5)
    c: DistanceY(g7,g6) = 3
    c: Symmetric(g0,g1,g9)
    c: Coincident(g11,g12)
    c: Coincident(g12,g13)
    c: Coincident(g13,g10)
    c: Horizontal(g10)
    c: Vertical(g11)
    c: Vertical(g13)
    c: Coincident(g10,g11)
    c: Coincident(g11,g7)
    c: Radius(g4) = 4
    c: Symmetric(g12,g10,g9)
    c: DistanceX(g10,g10) = 5
    c: Vertical(g2)
    c: DistanceY(g-1,g1) = 7.5
    c: DistanceY(g1,g0) = 27
    c: PointOnObject(g1,g2)
    c: Coincident(g15,g10)
    c: Coincident(g15,g12)
    c: Coincident(g14,g6)
    c: Coincident(g14,g10)
    c: Coincident(g17,g15)
    c: Coincident(g16,g7)
    c: Coincident(g18,g10)
    c: Coincident(g19,g15)
    c: Coincident(g20,g6)
    c: Coincident(g20,g18)
    c: Radius(g3) = 4
    c: Coincident(g4,g17)
    c: Coincident(g16,g4)
    c: Coincident(g18,g3)
    c: Coincident(g19,g3)
    c: Tangent(g3,g18) = -1.5708
    c: Tangent(g3,g19) = 1.5708
    c: Tangent(g4,g16) = 1.5708
    c: Tangent(g4,g17) = -1.5708
    c: Horizontal(g12)
    c: DistanceX(g-1,g15) = 13
    c: PointOnObject(g21,g5)
    c: DistanceX(g2,g21) = 15
    c: Radius(g21) = 4
    c: Coincident(g6,g21)
    c: Coincident(g7,g21)
    c: Radius(g22) = 3.25
    c: Coincident(g22,g21)
FEATURE [PartDesign::Pad] Pad049
  Length = 2
  Length2 = 100
  Profile = -> Sketch061
  Type = 0
FEATURE [PartDesign::Body] Body065  label="Hüllen001"
  Group = -> [Sketch061,Pad049]
  Origin = -> Origin110
  Placement = pos=(0,0,6) rot=(0,0,1;0rad)
  Tip = -> Pad049
FEATURE [Sketcher::SketchObject] Sketch063  label="Sketch064"
  MapMode = 5
  Support = -> [XY_Plane112]
  sketch-geometry (10):
    g0: LineSegment [constr] StartX=-6.93237 StartY=15.5 StartZ=0 EndX=36.7388 EndY=15.5 EndZ=0
    g1: LineSegment [constr] StartX=29 StartY=24.6884 StartZ=0 EndX=29 EndY=7.47839 EndZ=0
    g2: LineSegment StartX=14 StartY=17 StartZ=0 EndX=22 EndY=17 EndZ=0
    g3: LineSegment [constr] StartX=22 StartY=17 StartZ=0 EndX=22 EndY=14 EndZ=0
    g4: LineSegment StartX=22 StartY=14 StartZ=0 EndX=14 EndY=14 EndZ=0
    g5: LineSegment StartX=14 StartY=14 StartZ=0 EndX=14 EndY=17 EndZ=0
    g6: ArcOfCircle CenterX=29 CenterY=15.5 CenterZ=0 NormalX=0 NormalY=0 NormalZ=1 AngleXU=0 Radius=3 StartAngle=4.49107 EndAngle=8.0753
    g7: Circle CenterX=29 CenterY=15.5 CenterZ=0 NormalX=0 NormalY=0 NormalZ=1 AngleXU=0 Radius=1.6
    g8: LineSegment StartX=22 StartY=14 StartZ=0 EndX=28.3415 EndY=12.5732 EndZ=0
    g9: LineSegment StartX=22 StartY=17 StartZ=0 EndX=28.3415 EndY=18.4268 EndZ=0
  constraints (27):
    c: Horizontal(g0)
    c: DistanceY(g-1,g0) = 15.5
    c: Vertical(g1)
    c: DistanceX(g-1,g1) = 29
    c: Coincident(g2,g3)
    c: Coincident(g3,g4)
    c: Coincident(g4,g5)
    c: Coincident(g5,g2)
    c: Horizontal(g2)
    c: Horizontal(g4)
    c: Vertical(g3)
    c: Symmetric(g2,g4,g0)
    c: DistanceX(g-1,g4) = 14
    c: DistanceX(g4,g3) = 8
    c: PointOnObject(g6,g0)
    c: PointOnObject(g6,g1)
    c: Radius(g6) = 3
    c: Radius(g7) = 1.6
    c: PointOnObject(g7,g0)
    c: PointOnObject(g7,g1)
    c: Coincident(g9,g2)
    c: DistanceY(g5,g5) = 3
    c: Coincident(g8,g4)
    c: Coincident(g8,g6)
    c: Coincident(g9,g6)
    c: Tangent(g6,g9) = 1.5708
    c: Tangent(g6,g8) = -1.5708
FEATURE [PartDesign::Pad] Pad051
  Length = 2
  Length2 = 100
  Profile = -> Sketch063
  Type = 0
FEATURE [PartDesign::Body] Body067  label="Center_001"
  Group = -> [Sketch063,Pad051]
  Origin = -> Origin112
  Placement = pos=(0,0,8) rot=(0,0,1;0rad)
  Tip = -> Pad051
FEATURE [Part::Box] Box041  label="versteifung001"
  AttacherType = Attacher::AttachEngine3D
  Height = 2
  Length = 1.6
  Placement = pos=(14,11,8) rot=(0,0,1;0rad)
  Width = 20
FEATURE [Sketcher::SketchObject] Sketch064  label="Sketch065"
  MapMode = 5
  Support = -> [XY_Plane113]
  sketch-geometry (2):
    g0: Circle CenterX=14 CenterY=7.5 CenterZ=0 NormalX=0 NormalY=0 NormalZ=1 AngleXU=0 Radius=4
    g1: Circle CenterX=14 CenterY=7.5 CenterZ=0 NormalX=0 NormalY=0 NormalZ=1 AngleXU=0 Radius=1.6
  constraints (5):
    c: DistanceY(g-1,g0) = 7.5
    c: DistanceX(g-1,g0) = 14
    c: Coincident(g1,g0)
    c: Radius(g0) = 4
    c: Radius(g1) = 1.6
FEATURE [PartDesign::Pad] Pad052
  Length = 1
  Length2 = 100
  Profile = -> Sketch064
  Type = 0
FEATURE [Sketcher::SketchObject] Sketch065  label="Sketch066"
  MapMode = 5
  Support = -> [XY_Plane114]
  sketch-geometry (2):
    g0: Circle CenterX=14 CenterY=7.5 CenterZ=0 NormalX=0 NormalY=0 NormalZ=1 AngleXU=0 Radius=4
    g1: Circle CenterX=14 CenterY=7.5 CenterZ=0 NormalX=0 NormalY=0 NormalZ=1 AngleXU=0 Radius=1.6
  constraints (5):
    c: DistanceY(g-1,g0) = 7.5
    c: DistanceX(g-1,g0) = 14
    c: Coincident(g1,g0)
    c: Radius(g0) = 4
    c: Radius(g1) = 1.6
FEATURE [PartDesign::Pad] Pad053
  Length = 1
  Length2 = 100
  Profile = -> Sketch065
  Type = 0
FEATURE [Sketcher::SketchObject] Sketch066  label="Sketch067"
  MapMode = 5
  Support = -> [XY_Plane115]
  sketch-geometry (2):
    g0: Circle CenterX=14 CenterY=7.5 CenterZ=0 NormalX=0 NormalY=0 NormalZ=1 AngleXU=0 Radius=4
    g1: Circle CenterX=14 CenterY=7.5 CenterZ=0 NormalX=0 NormalY=0 NormalZ=1 AngleXU=0 Radius=1.6
  constraints (5):
    c: DistanceY(g-1,g0) = 7.5
    c: DistanceX(g-1,g0) = 14
    c: Coincident(g1,g0)
    c: Radius(g0) = 4
    c: Radius(g1) = 1.6
FEATURE [PartDesign::Pad] Pad054
  Length = 1
  Length2 = 100
  Profile = -> Sketch066
  Type = 0
FEATURE [PartDesign::Body] Body068  label="ab_S005"
  Group = -> [Sketch064,Pad052]
  Origin = -> Origin113
  Placement = pos=(0,0,8) rot=(0,0,1;0rad)
  Tip = -> Pad052
FEATURE [PartDesign::Body] Body069  label="ab_N004"
  Group = -> [Sketch065,Pad053]
  Origin = -> Origin114
  Placement = pos=(0,27,8) rot=(0,0,1;0rad)
  Tip = -> Pad053
FEATURE [PartDesign::Body] Body070  label="ab_C005"
  Group = -> [Sketch066,Pad054]
  Origin = -> Origin115
  Placement = pos=(15,8,8) rot=(0,0,1;0rad)
  Tip = -> Pad054
FEATURE [App::DocumentObjectGroup] Group032  label="abdeckung001"
  Group = -> [Body068,Body069,Body070]
FEATURE [Sketcher::SketchObject] Sketch067  label="Sketch068"
  MapMode = 5
  Support = -> [XY_Plane117]
  sketch-geometry (23):
    g0: Circle CenterX=14 CenterY=34.5 CenterZ=0 NormalX=0 NormalY=0 NormalZ=1 AngleXU=0 Radius=3.25
    g1: Circle CenterX=14 CenterY=7.5 CenterZ=0 NormalX=0 NormalY=0 NormalZ=1 AngleXU=0 Radius=3.25
    g2: LineSegment [constr] StartX=14 StartY=48.9156 StartZ=0 EndX=14 EndY=-5.6741 EndZ=0
    g3: ArcOfCircle CenterX=14 CenterY=34.5 CenterZ=0 NormalX=0 NormalY=0 NormalZ=1 AngleXU=0 Radius=4 StartAngle=6e-16 EndAngle=3.64277
    g4: ArcOfCircle CenterX=14 CenterY=7.5 CenterZ=0 NormalX=0 NormalY=0 NormalZ=1 AngleXU=0 Radius=4 StartAngle=2.64041 EndAngle=6.28319
    g5: LineSegment [constr] StartX=-8.91239 StartY=15.5 StartZ=0 EndX=34.8006 EndY=15.5 EndZ=0
    g6: LineSegment StartX=18 StartY=17 StartZ=0 EndX=25.2919 EndY=17 EndZ=0
    g7: LineSegment StartX=25.2919 StartY=14 StartZ=0 EndX=18 EndY=14 EndZ=0
    g8: LineSegment [constr] StartX=18 StartY=14 StartZ=0 EndX=18 EndY=17 EndZ=0
    g9: LineSegment [constr] StartX=-0.860876 StartY=21 StartZ=0 EndX=35.3843 EndY=21 EndZ=0
    g10: LineSegment [constr] StartX=13 StartY=28 StartZ=0 EndX=18 EndY=28 EndZ=0
    g11: LineSegment [constr] StartX=18 StartY=28 StartZ=0 EndX=18 EndY=14 EndZ=0
    g12: LineSegment [constr] StartX=18 StartY=14 StartZ=0 EndX=13 EndY=14 EndZ=0
    g13: LineSegment [constr] StartX=13 StartY=14 StartZ=0 EndX=13 EndY=28 EndZ=0
    g14: LineSegment [constr] StartX=18 StartY=28 StartZ=0 EndX=18 EndY=17 EndZ=0
    g15: LineSegment StartX=13 StartY=28 StartZ=0 EndX=13 EndY=14 EndZ=0
    g16: LineSegment StartX=18 StartY=14 StartZ=0 EndX=18 EndY=7.5 EndZ=0
    g17: LineSegment StartX=13 StartY=14 StartZ=0 EndX=10.4919 EndY=9.42184 EndZ=0
    g18: LineSegment StartX=18 StartY=28 StartZ=0 EndX=18 EndY=34.5 EndZ=0
    g19: LineSegment StartX=13 StartY=28 StartZ=0 EndX=10.4919 EndY=32.5782 EndZ=0
    g20: LineSegment StartX=18 StartY=28 StartZ=0 EndX=18 EndY=17 EndZ=0
    g21: ArcOfCircle CenterX=29 CenterY=15.5 CenterZ=0 NormalX=0 NormalY=0 NormalZ=1 AngleXU=0 Radius=4 StartAngle=3.52599 EndAngle=9.04038
    g22: Circle CenterX=29 CenterY=15.5 CenterZ=0 NormalX=0 NormalY=0 NormalZ=1 AngleXU=0 Radius=3.25
  constraints (57):
    c: Radius(g0) = 3.25
    c: Radius(g1) = 3.25
    c: Coincident(g0,g3)
    c: Coincident(g1,g4)
    c: DistanceX(g-1,g2) = 14
    c: Horizontal(g5)
    c: DistanceY(g-1,g5) = 15.5
    c: Coincident(g7,g8)
    c: Coincident(g8,g6)
    c: Horizontal(g6)
    c: Horizontal(g7)
    c: Symmetric(g7,g6,g5)
    c: DistanceY(g7,g6) = 3
    c: Symmetric(g0,g1,g9)
    c: Coincident(g11,g12)
    c: Coincident(g12,g13)
    c: Coincident(g13,g10)
    c: Horizontal(g10)
    c: Vertical(g11)
    c: Vertical(g13)
    c: Coincident(g10,g11)
    c: Coincident(g11,g7)
    c: Radius(g4) = 4
    c: Symmetric(g12,g10,g9)
    c: DistanceX(g10,g10) = 5
    c: Vertical(g2)
    c: DistanceY(g-1,g1) = 7.5
    c: DistanceY(g1,g0) = 27
    c: PointOnObject(g1,g2)
    c: Coincident(g15,g10)
    c: Coincident(g15,g12)
    c: Coincident(g14,g6)
    c: Coincident(g14,g10)
    c: Coincident(g17,g15)
    c: Coincident(g16,g7)
    c: Coincident(g18,g10)
    c: Coincident(g19,g15)
    c: Coincident(g20,g6)
    c: Coincident(g20,g18)
    c: Radius(g3) = 4
    c: Coincident(g4,g17)
    c: Coincident(g16,g4)
    c: Coincident(g18,g3)
    c: Coincident(g19,g3)
    c: Tangent(g3,g18) = -1.5708
    c: Tangent(g3,g19) = 1.5708
    c: Tangent(g4,g16) = 1.5708
    c: Tangent(g4,g17) = -1.5708
    c: Horizontal(g12)
    c: DistanceX(g-1,g15) = 13
    c: PointOnObject(g21,g5)
    c: DistanceX(g2,g21) = 15
    c: Radius(g21) = 4
    c: Coincident(g6,g21)
    c: Coincident(g7,g21)
    c: Radius(g22) = 3.25
    c: Coincident(g22,g21)
FEATURE [PartDesign::Pad] Pad055
  Length = 2
  Length2 = 100
  Profile = -> Sketch067
  Type = 0
FEATURE [Sketcher::SketchObject] Sketch068  label="Sketch069"
  MapMode = 5
  Support = -> [XY_Plane118]
  sketch-geometry (32):
    g0: LineSegment [constr] StartX=-2.78551 StartY=16.5 StartZ=0 EndX=35.9831 EndY=16.5 EndZ=0
    g1: LineSegment [constr] StartX=15.5 StartY=38.2848 StartZ=0 EndX=15.5 EndY=1.20933 EndZ=0
    g2: Circle CenterX=15.5 CenterY=22.25 CenterZ=0 NormalX=0 NormalY=0 NormalZ=1 AngleXU=0 Radius=0.75
    g3: Circle CenterX=15.5 CenterY=10.75 CenterZ=0 NormalX=0 NormalY=0 NormalZ=1 AngleXU=0 Radius=0.75
    g4: GeomPoint X=15.5 Y=10.75 Z=0
    g5: GeomPoint X=15.5 Y=22.25 Z=0
    g6: LineSegment [constr] StartX=13.1767 StartY=22.25 StartZ=0 EndX=17 EndY=22.25 EndZ=0
    g7: LineSegment [constr] StartX=17.8233 StartY=10.75 StartZ=0 EndX=13.1767 EndY=10.75 EndZ=0
    g8: LineSegment [constr] StartX=10.6454 StartY=10.75 StartZ=0 EndX=20.7493 EndY=10.75 EndZ=0
    g9: LineSegment [constr] StartX=12.0303 StartY=22.25 StartZ=0 EndX=19.3255 EndY=22.25 EndZ=0
    g10: LineSegment [constr] StartX=-4.22167 StartY=21 StartZ=0 EndX=42.5416 EndY=21 EndZ=0
    g11: Circle [constr] CenterX=14 CenterY=34.5 CenterZ=0 NormalX=0 NormalY=0 NormalZ=1 AngleXU=0 Radius=1.6
    g12: Circle [constr] CenterX=14 CenterY=7.5 CenterZ=0 NormalX=0 NormalY=0 NormalZ=1 AngleXU=0 Radius=1.6
    g13: LineSegment [constr] StartX=14 StartY=42.2647 StartZ=0 EndX=14 EndY=-1.81436 EndZ=0
    g14: LineSegment StartX=17 StartY=30.134 StartZ=0 EndX=17 EndY=31.866 EndZ=0
    g15: LineSegment StartX=17 StartY=31.866 StartZ=0 EndX=15.5 EndY=32.7321 EndZ=0
    g16: LineSegment StartX=15.5 StartY=32.7321 StartZ=0 EndX=14 EndY=31.866 EndZ=0
    g17: LineSegment StartX=14 StartY=31.866 StartZ=0 EndX=14 EndY=30.134 EndZ=0
    g18: LineSegment [constr] StartX=14 StartY=30.134 StartZ=0 EndX=15.5 EndY=29.2679 EndZ=0
    g19: LineSegment [constr] StartX=15.5 StartY=29.2679 StartZ=0 EndX=17 EndY=30.134 EndZ=0
    g20: Circle [constr] CenterX=15.5 CenterY=31 CenterZ=0 NormalX=0 NormalY=0 NormalZ=1 AngleXU=0 Radius=1.73205
    g21: LineSegment StartX=17 StartY=10.134 StartZ=0 EndX=17 EndY=11.866 EndZ=0
    g22: LineSegment [constr] StartX=17 StartY=11.866 StartZ=0 EndX=15.5 EndY=12.7321 EndZ=0
    g23: LineSegment [constr] StartX=15.5 StartY=12.7321 StartZ=0 EndX=14 EndY=11.866 EndZ=0
    g24: LineSegment StartX=14 StartY=11.866 StartZ=0 EndX=14 EndY=10.134 EndZ=0
    g25: LineSegment StartX=14 StartY=10.134 StartZ=0 EndX=15.5 EndY=9.26795 EndZ=0
    g26: LineSegment StartX=15.5 StartY=9.26795 StartZ=0 EndX=17 EndY=10.134 EndZ=0
    g27: Circle [constr] CenterX=15.5 CenterY=11 CenterZ=0 NormalX=0 NormalY=0 NormalZ=1 AngleXU=0 Radius=1.73205
    g28: LineSegment StartX=14 StartY=30.134 StartZ=0 EndX=14 EndY=11.866 EndZ=0
    g29: LineSegment StartX=17 StartY=30.134 StartZ=0 EndX=17 EndY=11.866 EndZ=0
    g30: Circle CenterX=15.5 CenterY=19.75 CenterZ=0 NormalX=0 NormalY=0 NormalZ=1 AngleXU=0 Radius=0.75
    g31: Circle CenterX=15.5 CenterY=31.25 CenterZ=0 NormalX=0 NormalY=0 NormalZ=1 AngleXU=0 Radius=0.75
  constraints (69):
    c: Vertical(g1)
    c: Horizontal(g0)
    c: DistanceX(g-1,g1) = 15.5
    c: Radius(g2) = 0.75
    c: Radius(g3) = 0.75
    c: PointOnObject(g3,g1)
    c: Symmetric(g2,g3,g0)
    c: DistanceY(g3,g2) = 11.5
    c: Coincident(g4,g3)
    c: Coincident(g5,g2)
    c: Horizontal(g6)
    c: Symmetric(g6,g7,g0)
    c: Symmetric(g7,g7,g1)
    c: PointOnObject(g3,g8)
    c: Horizontal(g8)
    c: PointOnObject(g7,g8)
    c: Horizontal(g9)
    c: PointOnObject(g2,g9)
    c: Horizontal(g10)
    c: Radius(g12) = 1.6
    c: Radius(g11) = 1.6
    c: Vertical(g13)
    c: PointOnObject(g11,g13)
    c: DistanceX(g-1,g13) = 14
    c: DistanceY(g12,g11) = 27
    c: Symmetric(g12,g11,g10)
    c: DistanceY(g-1,g10) = 21
    c: DistanceY(g0,g10) = 4.5
    c: Coincident(g14,g15)
    c: Coincident(g15,g16)
    c: Coincident(g16,g17)
    c: Coincident(g17,g18)
    c: Coincident(g18,g19)
    c: Coincident(g19,g14)
    c: Equal(g14, g15-g19) x5
    c: PointOnObject(g14,g20)
    c: PointOnObject(g15,g20)
    c: PointOnObject(g16,g20)
    c: PointOnObject(g17,g20)
    c: PointOnObject(g18,g20)
    c: PointOnObject(g19,g20)
    c: Coincident(g21,g22)
    c: Coincident(g22,g23)
    c: Coincident(g23,g24)
    c: Coincident(g24,g25)
    c: Coincident(g25,g26)
    c: Coincident(g26,g21)
    c: Equal(g21, g22-g26) x5
    c: PointOnObject(g21,g27)
    c: PointOnObject(g22,g27)
    c: PointOnObject(g23,g27)
    c: PointOnObject(g24,g27)
    c: PointOnObject(g25,g27)
    c: PointOnObject(g26,g27)
    c: PointOnObject(g20,g1)
    c: PointOnObject(g18,g1)
    c: PointOnObject(g25,g1)
    c: Symmetric(g27,g20,g10)
    c: DistanceY(g27,g20) = 20
    c: Coincident(g29,g14)
    c: Coincident(g28,g17)
    c: Coincident(g29,g21)
    c: Coincident(g28,g23)
    c: DistanceX(g17,g14) = 3
    c: Vertical(g28)
    c: Radius(g31) = 0.75
    c: Radius(g30) = 0.75
    c: Symmetric(g2,g30,g10)
    c: Symmetric(g31,g3,g10)
FEATURE [PartDesign::Pad] Pad056
  Length = 6
  Length2 = 100
  Profile = -> Sketch068
  Type = 0
FEATURE [PartDesign::Body] Body071  label="Hüllen002"
  Group = -> [Sketch067,Pad055]
  Origin = -> Origin117
  Placement = pos=(0,0,6) rot=(0,0,1;0rad)
  Tip = -> Pad055
FEATURE [PartDesign::Body] Body072  label="Täger002"
  Group = -> [Sketch068,Pad056]
  Origin = -> Origin118
  Placement = pos=(0.5,0,8) rot=(0,0,1;0rad)
  Tip = -> Pad056
FEATURE [Sketcher::SketchObject] Sketch069  label="Sketch070"
  MapMode = 5
  Support = -> [XY_Plane119]
  sketch-geometry (10):
    g0: LineSegment [constr] StartX=-6.93237 StartY=15.5 StartZ=0 EndX=36.7388 EndY=15.5 EndZ=0
    g1: LineSegment [constr] StartX=29 StartY=24.6884 StartZ=0 EndX=29 EndY=7.47839 EndZ=0
    g2: LineSegment StartX=14 StartY=17 StartZ=0 EndX=22 EndY=17 EndZ=0
    g3: LineSegment [constr] StartX=22 StartY=17 StartZ=0 EndX=22 EndY=14 EndZ=0
    g4: LineSegment StartX=22 StartY=14 StartZ=0 EndX=14 EndY=14 EndZ=0
    g5: LineSegment StartX=14 StartY=14 StartZ=0 EndX=14 EndY=17 EndZ=0
    g6: ArcOfCircle CenterX=29 CenterY=15.5 CenterZ=0 NormalX=0 NormalY=0 NormalZ=1 AngleXU=0 Radius=3 StartAngle=4.49107 EndAngle=8.0753
    g7: Circle CenterX=29 CenterY=15.5 CenterZ=0 NormalX=0 NormalY=0 NormalZ=1 AngleXU=0 Radius=1.6
    g8: LineSegment StartX=22 StartY=14 StartZ=0 EndX=28.3415 EndY=12.5732 EndZ=0
    g9: LineSegment StartX=22 StartY=17 StartZ=0 EndX=28.3415 EndY=18.4268 EndZ=0
  constraints (27):
    c: Horizontal(g0)
    c: DistanceY(g-1,g0) = 15.5
    c: Vertical(g1)
    c: DistanceX(g-1,g1) = 29
    c: Coincident(g2,g3)
    c: Coincident(g3,g4)
    c: Coincident(g4,g5)
    c: Coincident(g5,g2)
    c: Horizontal(g2)
    c: Horizontal(g4)
    c: Vertical(g3)
    c: Symmetric(g2,g4,g0)
    c: DistanceX(g-1,g4) = 14
    c: DistanceX(g4,g3) = 8
    c: PointOnObject(g6,g0)
    c: PointOnObject(g6,g1)
    c: Radius(g6) = 3
    c: Radius(g7) = 1.6
    c: PointOnObject(g7,g0)
    c: PointOnObject(g7,g1)
    c: Coincident(g9,g2)
    c: DistanceY(g5,g5) = 3
    c: Coincident(g8,g4)
    c: Coincident(g8,g6)
    c: Coincident(g9,g6)
    c: Tangent(g6,g9) = 1.5708
    c: Tangent(g6,g8) = -1.5708
FEATURE [PartDesign::Pad] Pad057
  Length = 2
  Length2 = 100
  Profile = -> Sketch069
  Type = 0
FEATURE [PartDesign::Body] Body073  label="Center_002"
  Group = -> [Sketch069,Pad057]
  Origin = -> Origin119
  Placement = pos=(0,0,8) rot=(0,0,1;0rad)
  Tip = -> Pad057
FEATURE [Part::Box] Box042  label="versteifung002"
  AttacherType = Attacher::AttachEngine3D
  Height = 2
  Length = 1.6
  Placement = pos=(14,11,8) rot=(0,0,1;0rad)
  Width = 20
FEATURE [Sketcher::SketchObject] Sketch070  label="Sketch071"
  MapMode = 5
  Support = -> [XY_Plane120]
  sketch-geometry (2):
    g0: Circle CenterX=14 CenterY=7.5 CenterZ=0 NormalX=0 NormalY=0 NormalZ=1 AngleXU=0 Radius=4
    g1: Circle CenterX=14 CenterY=7.5 CenterZ=0 NormalX=0 NormalY=0 NormalZ=1 AngleXU=0 Radius=1.6
  constraints (5):
    c: DistanceY(g-1,g0) = 7.5
    c: DistanceX(g-1,g0) = 14
    c: Coincident(g1,g0)
    c: Radius(g0) = 4
    c: Radius(g1) = 1.6
FEATURE [PartDesign::Pad] Pad058
  Length = 1
  Length2 = 100
  Profile = -> Sketch070
  Type = 0
FEATURE [Sketcher::SketchObject] Sketch071  label="Sketch072"
  MapMode = 5
  Support = -> [XY_Plane121]
  sketch-geometry (2):
    g0: Circle CenterX=14 CenterY=7.5 CenterZ=0 NormalX=0 NormalY=0 NormalZ=1 AngleXU=0 Radius=4
    g1: Circle CenterX=14 CenterY=7.5 CenterZ=0 NormalX=0 NormalY=0 NormalZ=1 AngleXU=0 Radius=1.6
  constraints (5):
    c: DistanceY(g-1,g0) = 7.5
    c: DistanceX(g-1,g0) = 14
    c: Coincident(g1,g0)
    c: Radius(g0) = 4
    c: Radius(g1) = 1.6
FEATURE [PartDesign::Pad] Pad059
  Length = 1
  Length2 = 100
  Profile = -> Sketch071
  Type = 0
FEATURE [Sketcher::SketchObject] Sketch072  label="Sketch074"
  MapMode = 5
  Support = -> [XY_Plane122]
  sketch-geometry (2):
    g0: Circle CenterX=14 CenterY=7.5 CenterZ=0 NormalX=0 NormalY=0 NormalZ=1 AngleXU=0 Radius=4
    g1: Circle CenterX=14 CenterY=7.5 CenterZ=0 NormalX=0 NormalY=0 NormalZ=1 AngleXU=0 Radius=1.6
  constraints (5):
    c: DistanceY(g-1,g0) = 7.5
    c: DistanceX(g-1,g0) = 14
    c: Coincident(g1,g0)
    c: Radius(g0) = 4
    c: Radius(g1) = 1.6
FEATURE [PartDesign::Pad] Pad060
  Length = 1
  Length2 = 100
  Profile = -> Sketch072
  Type = 0
FEATURE [PartDesign::Body] Body074  label="ab_S006"
  Group = -> [Sketch070,Pad058]
  Origin = -> Origin120
  Placement = pos=(0,0,8) rot=(0,0,1;0rad)
  Tip = -> Pad058
FEATURE [PartDesign::Body] Body075  label="ab_N005"
  Group = -> [Sketch071,Pad059]
  Origin = -> Origin121
  Placement = pos=(0,27,8) rot=(0,0,1;0rad)
  Tip = -> Pad059
FEATURE [PartDesign::Body] Body076  label="ab_C006"
  Group = -> [Sketch072,Pad060]
  Origin = -> Origin122
  Placement = pos=(15,8,8) rot=(0,0,1;0rad)
  Tip = -> Pad060
FEATURE [App::DocumentObjectGroup] Group033  label="abdeckung002"
  Group = -> [Body074,Body075,Body076]
FEATURE [App::Part] Part020  label="Träger_W001"
  Group = -> [Body071,Body072,Body073,Group033,Body074,Body075,Body076,Box042]
  Origin = -> Origin116
  Placement = pos=(0,0,-2) rot=(0,0,1;0rad)
FEATURE [Part::Box] Box043  label="versteifung003"
  AttacherType = Attacher::AttachEngine3D
  Height = 2
  Length = 1.6
  Placement = pos=(14,11,8) rot=(0,0,1;0rad)
  Width = 20
FEATURE [Sketcher::SketchObject] Sketch073  label="Sketch075"
  MapMode = 5
  Support = -> [XY_Plane124]
  sketch-geometry (32):
    g0: LineSegment [constr] StartX=-2.78551 StartY=16.5 StartZ=0 EndX=35.9831 EndY=16.5 EndZ=0
    g1: LineSegment [constr] StartX=15.5 StartY=38.2848 StartZ=0 EndX=15.5 EndY=1.20933 EndZ=0
    g2: Circle CenterX=15.5 CenterY=22.25 CenterZ=0 NormalX=0 NormalY=0 NormalZ=1 AngleXU=0 Radius=0.75
    g3: Circle CenterX=15.5 CenterY=10.75 CenterZ=0 NormalX=0 NormalY=0 NormalZ=1 AngleXU=0 Radius=0.75
    g4: GeomPoint X=15.5 Y=10.75 Z=0
    g5: GeomPoint X=15.5 Y=22.25 Z=0
    g6: LineSegment [constr] StartX=13.1767 StartY=22.25 StartZ=0 EndX=17 EndY=22.25 EndZ=0
    g7: LineSegment [constr] StartX=17.8233 StartY=10.75 StartZ=0 EndX=13.1767 EndY=10.75 EndZ=0
    g8: LineSegment [constr] StartX=10.6454 StartY=10.75 StartZ=0 EndX=20.7493 EndY=10.75 EndZ=0
    g9: LineSegment [constr] StartX=12.0303 StartY=22.25 StartZ=0 EndX=19.3255 EndY=22.25 EndZ=0
    g10: LineSegment [constr] StartX=-4.22167 StartY=21 StartZ=0 EndX=42.5416 EndY=21 EndZ=0
    g11: Circle [constr] CenterX=14 CenterY=34.5 CenterZ=0 NormalX=0 NormalY=0 NormalZ=1 AngleXU=0 Radius=1.6
    g12: Circle [constr] CenterX=14 CenterY=7.5 CenterZ=0 NormalX=0 NormalY=0 NormalZ=1 AngleXU=0 Radius=1.6
    g13: LineSegment [constr] StartX=14 StartY=42.2647 StartZ=0 EndX=14 EndY=-1.81436 EndZ=0
    g14: LineSegment StartX=17 StartY=30.134 StartZ=0 EndX=17 EndY=31.866 EndZ=0
    g15: LineSegment StartX=17 StartY=31.866 StartZ=0 EndX=15.5 EndY=32.7321 EndZ=0
    g16: LineSegment StartX=15.5 StartY=32.7321 StartZ=0 EndX=14 EndY=31.866 EndZ=0
    g17: LineSegment StartX=14 StartY=31.866 StartZ=0 EndX=14 EndY=30.134 EndZ=0
    g18: LineSegment [constr] StartX=14 StartY=30.134 StartZ=0 EndX=15.5 EndY=29.2679 EndZ=0
    g19: LineSegment [constr] StartX=15.5 StartY=29.2679 StartZ=0 EndX=17 EndY=30.134 EndZ=0
    g20: Circle [constr] CenterX=15.5 CenterY=31 CenterZ=0 NormalX=0 NormalY=0 NormalZ=1 AngleXU=0 Radius=1.73205
    g21: LineSegment StartX=17 StartY=10.134 StartZ=0 EndX=17 EndY=11.866 EndZ=0
    g22: LineSegment [constr] StartX=17 StartY=11.866 StartZ=0 EndX=15.5 EndY=12.7321 EndZ=0
    g23: LineSegment [constr] StartX=15.5 StartY=12.7321 StartZ=0 EndX=14 EndY=11.866 EndZ=0
    g24: LineSegment StartX=14 StartY=11.866 StartZ=0 EndX=14 EndY=10.134 EndZ=0
    g25: LineSegment StartX=14 StartY=10.134 StartZ=0 EndX=15.5 EndY=9.26795 EndZ=0
    g26: LineSegment StartX=15.5 StartY=9.26795 StartZ=0 EndX=17 EndY=10.134 EndZ=0
    g27: Circle [constr] CenterX=15.5 CenterY=11 CenterZ=0 NormalX=0 NormalY=0 NormalZ=1 AngleXU=0 Radius=1.73205
    g28: LineSegment StartX=14 StartY=30.134 StartZ=0 EndX=14 EndY=11.866 EndZ=0
    g29: LineSegment StartX=17 StartY=30.134 StartZ=0 EndX=17 EndY=11.866 EndZ=0
    g30: Circle CenterX=15.5 CenterY=19.75 CenterZ=0 NormalX=0 NormalY=0 NormalZ=1 AngleXU=0 Radius=0.75
    g31: Circle CenterX=15.5 CenterY=31.25 CenterZ=0 NormalX=0 NormalY=0 NormalZ=1 AngleXU=0 Radius=0.75
  constraints (69):
    c: Vertical(g1)
    c: Horizontal(g0)
    c: DistanceX(g-1,g1) = 15.5
    c: Radius(g2) = 0.75
    c: Radius(g3) = 0.75
    c: PointOnObject(g3,g1)
    c: Symmetric(g2,g3,g0)
    c: DistanceY(g3,g2) = 11.5
    c: Coincident(g4,g3)
    c: Coincident(g5,g2)
    c: Horizontal(g6)
    c: Symmetric(g6,g7,g0)
    c: Symmetric(g7,g7,g1)
    c: PointOnObject(g3,g8)
    c: Horizontal(g8)
    c: PointOnObject(g7,g8)
    c: Horizontal(g9)
    c: PointOnObject(g2,g9)
    c: Horizontal(g10)
    c: Radius(g12) = 1.6
    c: Radius(g11) = 1.6
    c: Vertical(g13)
    c: PointOnObject(g11,g13)
    c: DistanceX(g-1,g13) = 14
    c: DistanceY(g12,g11) = 27
    c: Symmetric(g12,g11,g10)
    c: DistanceY(g-1,g10) = 21
    c: DistanceY(g0,g10) = 4.5
    c: Coincident(g14,g15)
    c: Coincident(g15,g16)
    c: Coincident(g16,g17)
    c: Coincident(g17,g18)
    c: Coincident(g18,g19)
    c: Coincident(g19,g14)
    c: Equal(g14, g15-g19) x5
    c: PointOnObject(g14,g20)
    c: PointOnObject(g15,g20)
    c: PointOnObject(g16,g20)
    c: PointOnObject(g17,g20)
    c: PointOnObject(g18,g20)
    c: PointOnObject(g19,g20)
    c: Coincident(g21,g22)
    c: Coincident(g22,g23)
    c: Coincident(g23,g24)
    c: Coincident(g24,g25)
    c: Coincident(g25,g26)
    c: Coincident(g26,g21)
    c: Equal(g21, g22-g26) x5
    c: PointOnObject(g21,g27)
    c: PointOnObject(g22,g27)
    c: PointOnObject(g23,g27)
    c: PointOnObject(g24,g27)
    c: PointOnObject(g25,g27)
    c: PointOnObject(g26,g27)
    c: PointOnObject(g20,g1)
    c: PointOnObject(g18,g1)
    c: PointOnObject(g25,g1)
    c: Symmetric(g27,g20,g10)
    c: DistanceY(g27,g20) = 20
    c: Coincident(g29,g14)
    c: Coincident(g28,g17)
    c: Coincident(g29,g21)
    c: Coincident(g28,g23)
    c: DistanceX(g17,g14) = 3
    c: Vertical(g28)
    c: Radius(g31) = 0.75
    c: Radius(g30) = 0.75
    c: Symmetric(g2,g30,g10)
    c: Symmetric(g31,g3,g10)
FEATURE [PartDesign::Pad] Pad065
  Length = 6
  Length2 = 100
  Profile = -> Sketch073
  Type = 0
FEATURE [PartDesign::Body] Body078  label="Täger003"
  Group = -> [Sketch073,Pad065]
  Origin = -> Origin127
  Placement = pos=(0.5,0,8) rot=(0,0,1;0rad)
  Tip = -> Pad065
FEATURE [Sketcher::SketchObject] Sketch074  label="Sketch073"
  MapMode = 5
  Support = -> [XY_Plane126]
  sketch-geometry (23):
    g0: Circle CenterX=14 CenterY=34.5 CenterZ=0 NormalX=0 NormalY=0 NormalZ=1 AngleXU=0 Radius=3.25
    g1: Circle CenterX=14 CenterY=7.5 CenterZ=0 NormalX=0 NormalY=0 NormalZ=1 AngleXU=0 Radius=3.25
    g2: LineSegment [constr] StartX=14 StartY=48.9156 StartZ=0 EndX=14 EndY=-5.6741 EndZ=0
    g3: ArcOfCircle CenterX=14 CenterY=34.5 CenterZ=0 NormalX=0 NormalY=0 NormalZ=1 AngleXU=0 Radius=4 StartAngle=6e-16 EndAngle=3.64277
    g4: ArcOfCircle CenterX=14 CenterY=7.5 CenterZ=0 NormalX=0 NormalY=0 NormalZ=1 AngleXU=0 Radius=4 StartAngle=2.64041 EndAngle=6.28319
    g5: LineSegment [constr] StartX=-8.91239 StartY=15.5 StartZ=0 EndX=34.8006 EndY=15.5 EndZ=0
    g6: LineSegment StartX=18 StartY=17 StartZ=0 EndX=25.2919 EndY=17 EndZ=0
    g7: LineSegment StartX=25.2919 StartY=14 StartZ=0 EndX=18 EndY=14 EndZ=0
    g8: LineSegment [constr] StartX=18 StartY=14 StartZ=0 EndX=18 EndY=17 EndZ=0
    g9: LineSegment [constr] StartX=-0.860876 StartY=21 StartZ=0 EndX=35.3843 EndY=21 EndZ=0
    g10: LineSegment [constr] StartX=13 StartY=28 StartZ=0 EndX=18 EndY=28 EndZ=0
    g11: LineSegment [constr] StartX=18 StartY=28 StartZ=0 EndX=18 EndY=14 EndZ=0
    g12: LineSegment [constr] StartX=18 StartY=14 StartZ=0 EndX=13 EndY=14 EndZ=0
    g13: LineSegment [constr] StartX=13 StartY=14 StartZ=0 EndX=13 EndY=28 EndZ=0
    g14: LineSegment [constr] StartX=18 StartY=28 StartZ=0 EndX=18 EndY=17 EndZ=0
    g15: LineSegment StartX=13 StartY=28 StartZ=0 EndX=13 EndY=14 EndZ=0
    g16: LineSegment StartX=18 StartY=14 StartZ=0 EndX=18 EndY=7.5 EndZ=0
    g17: LineSegment StartX=13 StartY=14 StartZ=0 EndX=10.4919 EndY=9.42184 EndZ=0
    g18: LineSegment StartX=18 StartY=28 StartZ=0 EndX=18 EndY=34.5 EndZ=0
    g19: LineSegment StartX=13 StartY=28 StartZ=0 EndX=10.4919 EndY=32.5782 EndZ=0
    g20: LineSegment StartX=18 StartY=28 StartZ=0 EndX=18 EndY=17 EndZ=0
    g21: ArcOfCircle CenterX=29 CenterY=15.5 CenterZ=0 NormalX=0 NormalY=0 NormalZ=1 AngleXU=0 Radius=4 StartAngle=3.52599 EndAngle=9.04038
    g22: Circle CenterX=29 CenterY=15.5 CenterZ=0 NormalX=0 NormalY=0 NormalZ=1 AngleXU=0 Radius=3.25
  constraints (57):
    c: Radius(g0) = 3.25
    c: Radius(g1) = 3.25
    c: Coincident(g0,g3)
    c: Coincident(g1,g4)
    c: DistanceX(g-1,g2) = 14
    c: Horizontal(g5)
    c: DistanceY(g-1,g5) = 15.5
    c: Coincident(g7,g8)
    c: Coincident(g8,g6)
    c: Horizontal(g6)
    c: Horizontal(g7)
    c: Symmetric(g7,g6,g5)
    c: DistanceY(g7,g6) = 3
    c: Symmetric(g0,g1,g9)
    c: Coincident(g11,g12)
    c: Coincident(g12,g13)
    c: Coincident(g13,g10)
    c: Horizontal(g10)
    c: Vertical(g11)
    c: Vertical(g13)
    c: Coincident(g10,g11)
    c: Coincident(g11,g7)
    c: Radius(g4) = 4
    c: Symmetric(g12,g10,g9)
    c: DistanceX(g10,g10) = 5
    c: Vertical(g2)
    c: DistanceY(g-1,g1) = 7.5
    c: DistanceY(g1,g0) = 27
    c: PointOnObject(g1,g2)
    c: Coincident(g15,g10)
    c: Coincident(g15,g12)
    c: Coincident(g14,g6)
    c: Coincident(g14,g10)
    c: Coincident(g17,g15)
    c: Coincident(g16,g7)
    c: Coincident(g18,g10)
    c: Coincident(g19,g15)
    c: Coincident(g20,g6)
    c: Coincident(g20,g18)
    c: Radius(g3) = 4
    c: Coincident(g4,g17)
    c: Coincident(g16,g4)
    c: Coincident(g18,g3)
    c: Coincident(g19,g3)
    c: Tangent(g3,g18) = -1.5708
    c: Tangent(g3,g19) = 1.5708
    c: Tangent(g4,g16) = 1.5708
    c: Tangent(g4,g17) = -1.5708
    c: Horizontal(g12)
    c: DistanceX(g-1,g15) = 13
    c: PointOnObject(g21,g5)
    c: DistanceX(g2,g21) = 15
    c: Radius(g21) = 4
    c: Coincident(g6,g21)
    c: Coincident(g7,g21)
    c: Radius(g22) = 3.25
    c: Coincident(g22,g21)
FEATURE [PartDesign::Pad] Pad063
  Length = 2
  Length2 = 100
  Profile = -> Sketch074
  Type = 0
FEATURE [PartDesign::Body] Body077  label="Hüllen003"
  Group = -> [Sketch074,Pad063]
  Origin = -> Origin125
  Placement = pos=(0,0,6) rot=(0,0,1;0rad)
  Tip = -> Pad063
FEATURE [Sketcher::SketchObject] Sketch075  label="Sketch076"
  MapMode = 5
  Support = -> [XY_Plane125]
  sketch-geometry (10):
    g0: LineSegment [constr] StartX=-6.93237 StartY=15.5 StartZ=0 EndX=36.7388 EndY=15.5 EndZ=0
    g1: LineSegment [constr] StartX=29 StartY=24.6884 StartZ=0 EndX=29 EndY=7.47839 EndZ=0
    g2: LineSegment StartX=14 StartY=17 StartZ=0 EndX=22 EndY=17 EndZ=0
    g3: LineSegment [constr] StartX=22 StartY=17 StartZ=0 EndX=22 EndY=14 EndZ=0
    g4: LineSegment StartX=22 StartY=14 StartZ=0 EndX=14 EndY=14 EndZ=0
    g5: LineSegment StartX=14 StartY=14 StartZ=0 EndX=14 EndY=17 EndZ=0
    g6: ArcOfCircle CenterX=29 CenterY=15.5 CenterZ=0 NormalX=0 NormalY=0 NormalZ=1 AngleXU=0 Radius=3 StartAngle=4.49107 EndAngle=8.0753
    g7: Circle CenterX=29 CenterY=15.5 CenterZ=0 NormalX=0 NormalY=0 NormalZ=1 AngleXU=0 Radius=1.6
    g8: LineSegment StartX=22 StartY=14 StartZ=0 EndX=28.3415 EndY=12.5732 EndZ=0
    g9: LineSegment StartX=22 StartY=17 StartZ=0 EndX=28.3415 EndY=18.4268 EndZ=0
  constraints (27):
    c: Horizontal(g0)
    c: DistanceY(g-1,g0) = 15.5
    c: Vertical(g1)
    c: DistanceX(g-1,g1) = 29
    c: Coincident(g2,g3)
    c: Coincident(g3,g4)
    c: Coincident(g4,g5)
    c: Coincident(g5,g2)
    c: Horizontal(g2)
    c: Horizontal(g4)
    c: Vertical(g3)
    c: Symmetric(g2,g4,g0)
    c: DistanceX(g-1,g4) = 14
    c: DistanceX(g4,g3) = 8
    c: PointOnObject(g6,g0)
    c: PointOnObject(g6,g1)
    c: Radius(g6) = 3
    c: Radius(g7) = 1.6
    c: PointOnObject(g7,g0)
    c: PointOnObject(g7,g1)
    c: Coincident(g9,g2)
    c: DistanceY(g5,g5) = 3
    c: Coincident(g8,g4)
    c: Coincident(g8,g6)
    c: Coincident(g9,g6)
    c: Tangent(g6,g9) = 1.5708
    c: Tangent(g6,g8) = -1.5708
FEATURE [PartDesign::Pad] Pad066
  Length = 2
  Length2 = 100
  Profile = -> Sketch075
  Type = 0
FEATURE [PartDesign::Body] Body082  label="Center_003"
  Group = -> [Sketch075,Pad066]
  Origin = -> Origin126
  Placement = pos=(0,0,8) rot=(0,0,1;0rad)
  Tip = -> Pad066
FEATURE [Sketcher::SketchObject] Sketch076  label="Sketch077"
  MapMode = 5
  Support = -> [XY_Plane123]
  sketch-geometry (2):
    g0: Circle CenterX=14 CenterY=7.5 CenterZ=0 NormalX=0 NormalY=0 NormalZ=1 AngleXU=0 Radius=4
    g1: Circle CenterX=14 CenterY=7.5 CenterZ=0 NormalX=0 NormalY=0 NormalZ=1 AngleXU=0 Radius=1.6
  constraints (5):
    c: DistanceY(g-1,g0) = 7.5
    c: DistanceX(g-1,g0) = 14
    c: Coincident(g1,g0)
    c: Radius(g0) = 4
    c: Radius(g1) = 1.6
FEATURE [PartDesign::Pad] Pad062
  Length = 1
  Length2 = 100
  Profile = -> Sketch076
  Type = 0
FEATURE [PartDesign::Body] Body079  label="ab_S007"
  Group = -> [Sketch076,Pad062]
  Origin = -> Origin129
  Placement = pos=(0,0,8) rot=(0,0,1;0rad)
  Tip = -> Pad062
FEATURE [Sketcher::SketchObject] Sketch077  label="Sketch078"
  MapMode = 5
  Support = -> [XY_Plane128]
  sketch-geometry (2):
    g0: Circle CenterX=14 CenterY=7.5 CenterZ=0 NormalX=0 NormalY=0 NormalZ=1 AngleXU=0 Radius=4
    g1: Circle CenterX=14 CenterY=7.5 CenterZ=0 NormalX=0 NormalY=0 NormalZ=1 AngleXU=0 Radius=1.6
  constraints (5):
    c: DistanceY(g-1,g0) = 7.5
    c: DistanceX(g-1,g0) = 14
    c: Coincident(g1,g0)
    c: Radius(g0) = 4
    c: Radius(g1) = 1.6
FEATURE [PartDesign::Pad] Pad064
  Length = 1
  Length2 = 100
  Profile = -> Sketch077
  Type = 0
FEATURE [PartDesign::Body] Body080  label="ab_N006"
  Group = -> [Sketch077,Pad064]
  Origin = -> Origin123
  Placement = pos=(0,27,8) rot=(0,0,1;0rad)
  Tip = -> Pad064
FEATURE [Sketcher::SketchObject] Sketch078  label="Sketch079"
  MapMode = 5
  Support = -> [XY_Plane129]
  sketch-geometry (2):
    g0: Circle CenterX=14 CenterY=7.5 CenterZ=0 NormalX=0 NormalY=0 NormalZ=1 AngleXU=0 Radius=4
    g1: Circle CenterX=14 CenterY=7.5 CenterZ=0 NormalX=0 NormalY=0 NormalZ=1 AngleXU=0 Radius=1.6
  constraints (5):
    c: DistanceY(g-1,g0) = 7.5
    c: DistanceX(g-1,g0) = 14
    c: Coincident(g1,g0)
    c: Radius(g0) = 4
    c: Radius(g1) = 1.6
FEATURE [PartDesign::Pad] Pad061
  Length = 1
  Length2 = 100
  Profile = -> Sketch078
  Type = 0
FEATURE [PartDesign::Body] Body081  label="ab_C007"
  Group = -> [Sketch078,Pad061]
  Origin = -> Origin128
  Placement = pos=(15,8,8) rot=(0,0,1;0rad)
  Tip = -> Pad061
FEATURE [App::DocumentObjectGroup] Group034  label="abdeckung003"
  Group = -> [Body079,Body080,Body081]
FEATURE [App::Part] Part021  label="Träger_O001"
  Group = -> [Body077,Body078,Body082,Group034,Body079,Body080,Body081,Box043]
  Origin = -> Origin124
  Placement = pos=(79,42,-2) rot=(0,0,1;3.14159rad)
FEATURE [App::DocumentObjectGroup] Gruppe073  label="Träger_symRespNano"
  Group = -> [Part021,Part020]
FEATURE [Sketcher::SketchObject] Sketch079  label="Sketch080"
  MapMode = 5
  Support = -> [XY_Plane131]
  sketch-geometry (10):
    g0: LineSegment StartX=0 StartY=0 StartZ=0 EndX=51.5 EndY=0 EndZ=0
    g1: LineSegment StartX=51.5 StartY=0 StartZ=0 EndX=51.5 EndY=28.2 EndZ=0
    g2: LineSegment StartX=51.5 StartY=28.2 StartZ=0 EndX=0 EndY=28.2 EndZ=0
    g3: LineSegment StartX=0 StartY=28.2 StartZ=0 EndX=0 EndY=0 EndZ=0
    g4: Circle CenterX=2.5 CenterY=25.6 CenterZ=0 NormalX=0 NormalY=0 NormalZ=1 AngleXU=0 Radius=1.4
    g5: Circle CenterX=2.5 CenterY=2.6 CenterZ=0 NormalX=0 NormalY=0 NormalZ=1 AngleXU=0 Radius=1.4
    g6: LineSegment [constr] StartX=-4.79847 StartY=14.1 StartZ=0 EndX=59.5233 EndY=14.1 EndZ=0
    g7: LineSegment [constr] StartX=25.75 StartY=32.5453 StartZ=0 EndX=25.75 EndY=-7.09199 EndZ=0
    g8: Circle CenterX=49 CenterY=25.6 CenterZ=0 NormalX=0 NormalY=0 NormalZ=1 AngleXU=0 Radius=1.4
    g9: Circle CenterX=49 CenterY=2.6 CenterZ=0 NormalX=0 NormalY=0 NormalZ=1 AngleXU=0 Radius=1.4
  constraints (22):
    c: Coincident(g0,g1)
    c: Coincident(g1,g2)
    c: Coincident(g2,g3)
    c: Coincident(g3,g0)
    c: Horizontal(g0)
    c: Horizontal(g2)
    c: Vertical(g1)
    c: Vertical(g3)
    c: DistanceY(g3,g3) = 28.2
    c: DistanceX(g0,g0) = 51.5
    c: Radius(g5) = 1.4
    c: Coincident(g0,g-1)
    c: Symmetric(g0,g2,g6)
    c: Symmetric(g5,g4,g6)
    c: DistanceY(g5,g4) = 23
    c: DistanceX(g0,g5) = 2.5
    c: Symmetric(g0,g0,g7)
    c: Symmetric(g8,g4,g7)
    c: Symmetric(g9,g5,g7)
    c: Equal(g5,g4)
    c: Equal(g4,g8)
    c: Equal(g8,g9)
FEATURE [PartDesign::Pad] Pad067
  Length = 1
  Length2 = 100
  Profile = -> Sketch079
  Type = 0
FEATURE [PartDesign::Body] Body083  label="plain"
  Group = -> [Sketch079,Pad067]
  Origin = -> Origin131
  Placement = pos=(16,5,10) rot=(0,0,1;0rad)
  Tip = -> Pad067
FEATURE [Part::Box] Box044  label="USB Connector002"
  AttacherType = Attacher::AttachEngine3D
  Height = 3
  Length = 6
  Placement = pos=(15.5,15.25,11) rot=(0,0,1;0rad)
  Width = 7.5
FEATURE [Sketcher::SketchObject] Sketch082  label="Sketch083"
  MapMode = 2
  Placement = pos=(-2.5,1,2) rot=(0,0,1;0rad)
  sketch-geometry (7):
    g0: LineSegment StartX=1.25 StartY=7.5 StartZ=0 EndX=5.75 EndY=7.5 EndZ=0
    g1: LineSegment StartX=5.75 StartY=7.5 StartZ=0 EndX=5.75 EndY=4.5 EndZ=0
    g2: LineSegment StartX=5.75 StartY=4.5 StartZ=0 EndX=1.25 EndY=4.5 EndZ=0
    g3: LineSegment StartX=1.25 StartY=4.5 StartZ=0 EndX=1.25 EndY=7.5 EndZ=0
    g4: LineSegment [constr] StartX=3.5 StartY=10.5286 StartZ=0 EndX=3.5 EndY=1.2978 EndZ=0
    g5: LineSegment [constr] StartX=-2.09195 StartY=6 StartZ=0 EndX=11.2706 EndY=6 EndZ=0
    g6: LineSegment [constr] StartX=-9.86071 StartY=14 StartZ=0 EndX=20.1535 EndY=14 EndZ=0
  constraints (16):
    c: Coincident(g0,g1)
    c: Coincident(g1,g2)
    c: Coincident(g2,g3)
    c: Coincident(g3,g0)
    c: Horizontal(g0)
    c: Horizontal(g2)
    c: Vertical(g1)
    c: Vertical(g3)
    c: DistanceY(g1,g1) = 3
    c: DistanceX(g2,g2) = 4.5
    c: Symmetric(g2,g0,g5)
    c: Symmetric(g1,g2,g4)
    c: DistanceX(g-1,g4) = 3.5
    c: Horizontal(g6)
    c: DistanceY(g-1,g6) = 14
    c: DistanceY(g5,g6) = 8
FEATURE [PartDesign::Pad] Pad070
  Length = 3.5
  Length2 = 100
  Placement = pos=(-2.5,1,2) rot=(0,0,1;0rad)
  Profile = -> Sketch082
  Type = 0
FEATURE [PartDesign::Body] Body088  label="Switch001"
  Group = -> [Sketch082,Pad070]
  Origin = -> Origin137
  Placement = pos=(18.75,4,8) rot=(0,0,1;0rad)
  Tip = -> Pad070
FEATURE [Sketcher::SketchObject] Sketch083  label="Sketch084"
  MapMode = 2
  Placement = pos=(-2.5,1,2) rot=(0,0,1;0rad)
  sketch-geometry (7):
    g0: LineSegment StartX=1.25 StartY=23.5 StartZ=0 EndX=5.75 EndY=23.5 EndZ=0
    g1: LineSegment StartX=5.75 StartY=23.5 StartZ=0 EndX=5.75 EndY=20.5 EndZ=0
    g2: LineSegment StartX=5.75 StartY=20.5 StartZ=0 EndX=1.25 EndY=20.5 EndZ=0
    g3: LineSegment StartX=1.25 StartY=20.5 StartZ=0 EndX=1.25 EndY=23.5 EndZ=0
    g4: LineSegment [constr] StartX=3.5 StartY=25.8901 StartZ=0 EndX=3.5 EndY=16.6594 EndZ=0
    g5: LineSegment [constr] StartX=-1.93443 StartY=22 StartZ=0 EndX=11.4282 EndY=22 EndZ=0
    g6: LineSegment [constr] StartX=-9.86071 StartY=14 StartZ=0 EndX=20.1535 EndY=14 EndZ=0
  constraints (16):
    c: Coincident(g0,g1)
    c: Coincident(g1,g2)
    c: Coincident(g2,g3)
    c: Coincident(g3,g0)
    c: Horizontal(g0)
    c: Horizontal(g2)
    c: Vertical(g1)
    c: Vertical(g3)
    c: DistanceY(g1,g1) = 3
    c: DistanceX(g2,g2) = 4.5
    c: Symmetric(g2,g0,g5)
    c: Symmetric(g1,g2,g4)
    c: DistanceX(g-1,g4) = 3.5
    c: Horizontal(g6)
    c: DistanceY(g-1,g6) = 14
    c: DistanceY(g6,g5) = 8
FEATURE [PartDesign::Pad] Pad071
  Length = 3.5
  Length2 = 100
  Placement = pos=(-2.5,1,2) rot=(0,0,1;0rad)
  Profile = -> Sketch083
  Type = 0
FEATURE [PartDesign::Body] Body089  label="Switch002"
  Group = -> [Sketch083,Pad071]
  Origin = -> Origin138
  Placement = pos=(18.75,4,8) rot=(0,0,1;0rad)
  Tip = -> Pad071
FEATURE [App::Part] Part024  label="platine001"
  Group = -> [Body083,Body088,Body089]
  Origin = -> Origin136
FEATURE [App::Part] Part022  label="ESP32"
  Group = -> [Box044,Part024]
  Origin = -> Origin130
  Placement = pos=(0,-1.5,2) rot=(0,0,1;0rad)
FEATURE [Sketcher::SketchObject] Sketch080  label="Sketch081"
  MapMode = 2
  Placement = pos=(0,-1.5,2) rot=(0,0,1;0rad)
  Support = -> [Part022]
  sketch-geometry (6):
    g0: LineSegment StartX=9.75 StartY=8.5 StartZ=0 EndX=14.25 EndY=8.5 EndZ=0
    g1: LineSegment StartX=14.25 StartY=8.5 StartZ=0 EndX=14.25 EndY=5.5 EndZ=0
    g2: LineSegment StartX=14.25 StartY=5.5 StartZ=0 EndX=9.75 EndY=5.5 EndZ=0
    g3: LineSegment StartX=9.75 StartY=5.5 StartZ=0 EndX=9.75 EndY=8.5 EndZ=0
    g4: LineSegment [constr] StartX=12 StartY=10.8276 StartZ=0 EndX=12 EndY=1.68736 EndZ=0
    g5: LineSegment [constr] StartX=5.39302 StartY=7 StartZ=0 EndX=18.7548 EndY=7 EndZ=0
  constraints (14):
    c: Coincident(g0,g1)
    c: Coincident(g1,g2)
    c: Coincident(g2,g3)
    c: Coincident(g3,g0)
    c: Horizontal(g0)
    c: Horizontal(g2)
    c: Vertical(g1)
    c: Vertical(g3)
    c: DistanceY(g1,g1) = 3
    c: DistanceX(g2,g2) = 4.5
    c: Symmetric(g2,g0,g5)
    c: Symmetric(g1,g2,g4)
    c: DistanceX(g-1,g4) = 12
    c: DistanceY(g-1,g5) = 7
FEATURE [PartDesign::Pad] Pad068
  Length = 3.5
  Length2 = 100
  Placement = pos=(0,-1.5,2) rot=(0,0,1;0rad)
  Profile = -> Sketch080
  Type = 0
FEATURE [PartDesign::Body] Body086  label="Switch0"
  Group = -> [Sketch080,Pad068]
  Origin = -> Origin134
  Placement = pos=(18.75,4,8) rot=(0,0,1;0rad)
  Tip = -> Pad068
FEATURE [App::Part] Part023  label="platine"
  Group = -> [Body047,Body086]
  Origin = -> Origin135
FEATURE [App::Part] Part015  label="Resp-Nano"
  Group = -> [Box039,Part023]
  Origin = -> Origin086
  Placement = pos=(-2.5,1,2) rot=(0,0,1;0rad)
FEATURE [App::DocumentObjectGroup] Gruppe057  label="Schaltungs-Folder"
  Group = -> [Part014,Part015,Part022]
FEATURE [Sketcher::SketchObject] Sketch084  label="Sketch085"
  MapMode = 5
  Support = -> [XY_Plane141]
  sketch-geometry (31):
    g0: LineSegment [constr] StartX=-2.78551 StartY=16.5 StartZ=0 EndX=35.9831 EndY=16.5 EndZ=0
    g1: LineSegment [constr] StartX=18.5 StartY=38.2848 StartZ=0 EndX=18.5 EndY=1.20933 EndZ=0
    g2: Circle CenterX=18.5 CenterY=7.25 CenterZ=0 NormalX=0 NormalY=0 NormalZ=1 AngleXU=0 Radius=0.75
    g3: GeomPoint X=18.5 Y=7.25 Z=0
    g4: GeomPoint X=18.6 Y=22.25 Z=0
    g5: LineSegment [constr] StartX=15.9862 StartY=20.9487 StartZ=0 EndX=17 EndY=20.9487 EndZ=0
    g6: LineSegment [constr] StartX=12.0303 StartY=22.25 StartZ=0 EndX=19.3255 EndY=22.25 EndZ=0
    g7: LineSegment [constr] StartX=-4.22167 StartY=21 StartZ=0 EndX=42.5416 EndY=21 EndZ=0
    g8: Circle [constr] CenterX=14 CenterY=34.5 CenterZ=0 NormalX=0 NormalY=0 NormalZ=1 AngleXU=0 Radius=1.6
    g9: Circle [constr] CenterX=14 CenterY=7.5 CenterZ=0 NormalX=0 NormalY=0 NormalZ=1 AngleXU=0 Radius=1.6
    g10: LineSegment [constr] StartX=14 StartY=42.2647 StartZ=0 EndX=14 EndY=-1.81436 EndZ=0
    g11: LineSegment StartX=20.5 StartY=29.7859 StartZ=0 EndX=20.5 EndY=32.0953 EndZ=0
    g12: LineSegment StartX=20.5 StartY=32.0953 StartZ=0 EndX=18.5 EndY=33.25 EndZ=0
    g13: LineSegment StartX=18.5 StartY=33.25 StartZ=0 EndX=16.5 EndY=32.0953 EndZ=0
    g14: LineSegment StartX=16.5 StartY=32.0953 StartZ=0 EndX=16.5 EndY=29.7859 EndZ=0
    g15: LineSegment [constr] StartX=16.5 StartY=29.7859 StartZ=0 EndX=18.5 EndY=28.6312 EndZ=0
    g16: LineSegment [constr] StartX=18.5 StartY=28.6312 StartZ=0 EndX=20.5 EndY=29.7859 EndZ=0
    g17: Circle [constr] CenterX=18.5 CenterY=30.9406 CenterZ=0 NormalX=0 NormalY=0 NormalZ=1 AngleXU=0 Radius=2.3094
    g18: LineSegment StartX=20.5 StartY=5.4047 StartZ=0 EndX=20.5 EndY=7.7141 EndZ=0
    g19: LineSegment [constr] StartX=20.5 StartY=7.7141 StartZ=0 EndX=18.5 EndY=8.8688 EndZ=0
    g20: LineSegment [constr] StartX=18.5 StartY=8.8688 StartZ=0 EndX=16.5 EndY=7.7141 EndZ=0
    g21: LineSegment StartX=16.5 StartY=7.7141 StartZ=0 EndX=16.5 EndY=5.4047 EndZ=0
    g22: LineSegment StartX=16.5 StartY=5.4047 StartZ=0 EndX=18.5 EndY=4.25 EndZ=0
    g23: LineSegment StartX=18.5 StartY=4.25 StartZ=0 EndX=20.5 EndY=5.4047 EndZ=0
    g24: Circle [constr] CenterX=18.5 CenterY=6.5594 CenterZ=0 NormalX=0 NormalY=0 NormalZ=1 AngleXU=0 Radius=2.3094
    g25: LineSegment StartX=16.5 StartY=29.7859 StartZ=0 EndX=16.5 EndY=7.7141 EndZ=0
    g26: LineSegment StartX=20.5 StartY=29.7859 StartZ=0 EndX=20.5 EndY=7.7141 EndZ=0
    g27: Circle CenterX=18.5 CenterY=30.25 CenterZ=0 NormalX=0 NormalY=0 NormalZ=1 AngleXU=0 Radius=0.75
    g28: LineSegment [constr] StartX=6.75266 StartY=18.75 StartZ=0 EndX=35.0336 EndY=18.75 EndZ=0
    g29: Circle CenterX=18.5 CenterY=26.5 CenterZ=0 NormalX=0 NormalY=0 NormalZ=1 AngleXU=0 Radius=0.75
    g30: Circle CenterX=18.5 CenterY=15 CenterZ=0 NormalX=0 NormalY=0 NormalZ=1 AngleXU=0 Radius=0.75
  constraints (66):
    c: Vertical(g1)
    c: Horizontal(g0)
    c: DistanceX(g-1,g1) = 18.5
    c: Radius(g2) = 0.75
    c: PointOnObject(g2,g1)
    c: Coincident(g3,g2)
    c: Horizontal(g5)
    c: Horizontal(g6)
    c: Horizontal(g7)
    c: Radius(g9) = 1.6
    c: Radius(g8) = 1.6
    c: Vertical(g10)
    c: PointOnObject(g8,g10)
    c: DistanceX(g-1,g10) = 14
    c: DistanceY(g9,g8) = 27
    c: Symmetric(g9,g8,g7)
    c: DistanceY(g-1,g7) = 21
    c: DistanceY(g0,g7) = 4.5
    c: Coincident(g11,g12)
    c: Coincident(g12,g13)
    c: Coincident(g13,g14)
    c: Coincident(g14,g15)
    c: Coincident(g15,g16)
    c: Coincident(g16,g11)
    c: Equal(g11, g12-g16) x5
    c: PointOnObject(g11,g17)
    c: PointOnObject(g12,g17)
    c: PointOnObject(g13,g17)
    c: PointOnObject(g14,g17)
    c: PointOnObject(g15,g17)
    c: PointOnObject(g16,g17)
    c: Coincident(g18,g19)
    c: Coincident(g19,g20)
    c: Coincident(g20,g21)
    c: Coincident(g21,g22)
    c: Coincident(g22,g23)
    c: Coincident(g23,g18)
    c: Equal(g18, g19-g23) x5
    c: PointOnObject(g18,g24)
    c: PointOnObject(g19,g24)
    c: PointOnObject(g20,g24)
    c: PointOnObject(g21,g24)
    c: PointOnObject(g22,g24)
    c: PointOnObject(g23,g24)
    c: PointOnObject(g17,g1)
    c: PointOnObject(g15,g1)
    c: PointOnObject(g22,g1)
    c: Coincident(g26,g11)
    c: Coincident(g25,g14)
    c: Coincident(g26,g18)
    c: Coincident(g25,g20)
    c: DistanceX(g14,g11) = 4
    c: Vertical(g25)
    c: Radius(g27) = 0.75
    c: Vertical(g26)
    c: DistanceY(g22,g12) = 29
    c: Symmetric(g15,g19,g28)
    c: Symmetric(g2,g27,g28)
    c: DistanceY(g22,g2) = 3
    c: DistanceY(g-1,g28) = 18.75
    c: Radius(g29) = 0.75
    c: Radius(g30) = 0.75
    c: DistanceY(g30,g29) = 11.5
    c: PointOnObject(g29,g1)
    c: PointOnObject(g30,g1)
    c: DistanceY(g29,g12) = 6.75
FEATURE [PartDesign::Pad] Pad072
  Length = 6
  Length2 = 100
  Profile = -> Sketch084
  Type = 0
FEATURE [PartDesign::Body] Body090  label="Täger004"
  Group = -> [Sketch084,Pad072]
  Origin = -> Origin139
  Placement = pos=(-3.5,4.7,8) rot=(0,0,1;0rad)
  Tip = -> Pad072
FEATURE [App::Part] Part019  label="Träger_O"
  Group = -> [Body065,Body067,Group032,Body068,Body069,Body070,Box041,Body090]
  Origin = -> Origin109
  Placement = pos=(79,42,-2) rot=(0,0,1;3.14159rad)
FEATURE [App::DocumentObjectGroup] Gruppe072  label="Träger_Esp32+"
  Group = -> [Part019,Part013]
FEATURE [App::DocumentObjectGroup] Group025  label="Träger_F"
  Group = -> [Gruppe072,Gruppe073]
FEATURE [App::DocumentObjectGroup] Gruppe075  label="respNano"
FEATURE [Mesh::Feature] Mesh  label="Hüllen (Meshed)"
FEATURE [Mesh::Feature] Mesh001  label="Täger (Meshed)"
FEATURE [Mesh::Feature] Mesh002  label="Center_00 (Meshed)"
FEATURE [Mesh::Feature] Mesh003  label="ab_S004 (Meshed)"
FEATURE [Mesh::Feature] Mesh004  label="Pad047 (Meshed)"
FEATURE [Mesh::Feature] Mesh005  label="ab_C004 (Meshed)"
FEATURE [Mesh::Feature] Mesh006  label="Hüllen001 (Meshed)"
FEATURE [Mesh::Feature] Mesh007  label="Center_001 (Meshed)"
FEATURE [Mesh::Feature] Mesh008  label="ab_S005 (Meshed)"
FEATURE [Mesh::Feature] Mesh009  label="ab_N004 (Meshed)"
FEATURE [Mesh::Feature] Mesh010  label="ab_C005 (Meshed)"
FEATURE [Mesh::Feature] Mesh011  label="Täger004 (Meshed)"
FEATURE [App::DocumentObjectGroup] Gruppe074  label="Esp32"
  Group = -> [Mesh,Mesh001,Mesh002,Mesh003,Mesh004,Mesh005,Mesh006,Mesh007,Mesh008,Mesh009,Mesh010,Mesh011]
FEATURE [Mesh::Feature] Mesh012  label="CB_Esp32+RespN_H166"
FEATURE [App::DocumentObjectGroup] Gruppe  label="Halter"
  Group = -> [Gruppe074,Gruppe075,Mesh012]
FEATURE [App::DocumentObjectGroup] Group011  label="Mesh"
  Group = -> [Gruppe]
